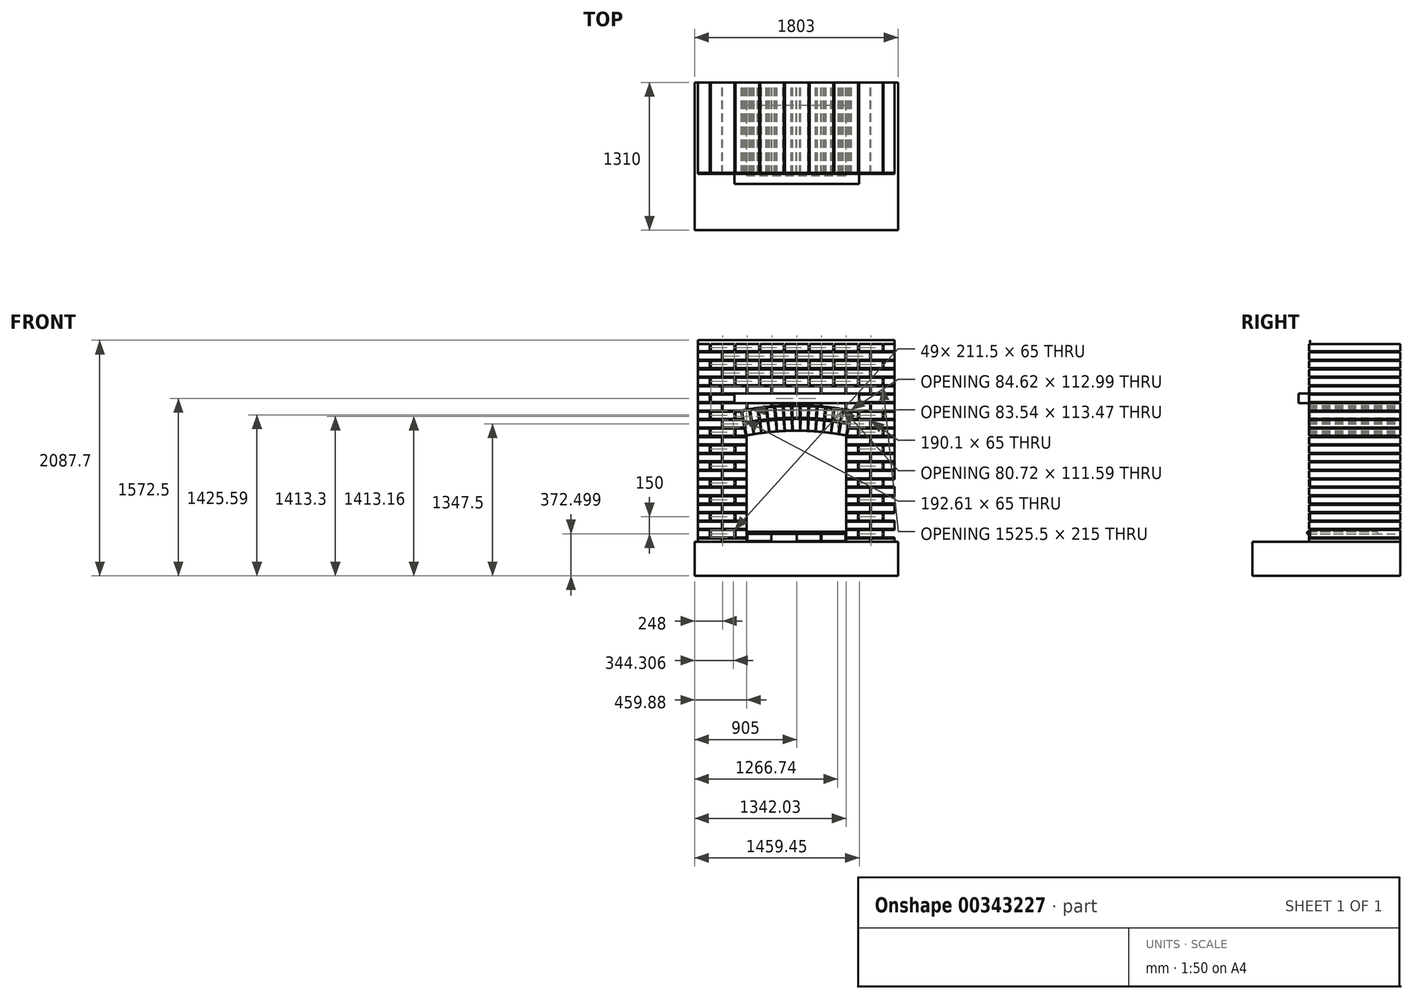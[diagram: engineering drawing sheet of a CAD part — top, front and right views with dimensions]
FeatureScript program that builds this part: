
annotation { "Feature Type Name" : "Feature", "Feature Type Description" : "" }
export const myFeature = defineFeature(function(context is Context, id is Id, definition is map)
    precondition{}
    {
        {
            var Q0;
            Q0=qCreatedBy(makeId("Front.planeOp"),FACE);
            var sketch = newSketch(context, id + "F0", { "sketchPlane" : qUnion([Q0])});
            skArc(sketch, "E0", {"start": v(-257.23, 343.57) * mm, "mid": v(-289.53, 339.93) * mm, "end": v(-321.78, 335.87) * mm});
            skArc(sketch, "E1", {"start": v(316.65, 324.44) * mm, "mid": v(284.4, 328.46) * mm, "end": v(252.09, 332.04) * mm});
            skArc(sketch, "E2", {"start": v(461.03, 301.03) * mm, "mid": v(428.59, 307.07) * mm, "end": v(396.06, 312.67) * mm});
            skArc(sketch, "E3", {"start": v(463.3, 312.82) * mm, "mid": v(430.8, 318.87) * mm, "end": v(398.22, 324.48) * mm});
            skLineSegment(sketch, "E4", {"start": v(547.25, 196.15) * mm, "end": v(448.41, 196.15) * mm});
            skLineSegment(sketch, "E5", {"start": v(547.25, 346.15) * mm, "end": v(477.38, 346.15) * mm});
            skLineSegment(sketch, "E6", {"start": v(901.5, -743.85) * mm, "end": v(-901.5, -743.85) * mm});
            skLineSegment(sketch, "E7", {"start": v(-872.5, -743.85) * mm, "end": v(-872.5, 1043.85) * mm});
            skLineSegment(sketch, "E8", {"start": v(901.5, -1043.85) * mm, "end": v(901.5, -743.85) * mm});
            skLineSegment(sketch, "E9", {"start": v(-901.5, -1043.85) * mm, "end": v(-901.5, -743.85) * mm});
            skLineSegment(sketch, "E10", {"start": v(901.5, -1043.85) * mm, "end": v(-901.5, -1043.85) * mm});
            skArc(sketch, "E11", {"start": v(441.5, 199.9) * mm, "mid": v(-0.25, 242.15) * mm, "end": v(-442, 199.8) * mm});
            skLineSegment(sketch, "E12", {"start": v(-75, 136.15) * mm, "end": v(-75, 240.94) * mm});
            skLineSegment(sketch, "E13", {"start": v(75, 136.15) * mm, "end": v(75, 240.94) * mm});
            skLineSegment(sketch, "E14", {"start": v(-661, 871.15) * mm, "end": v(-872.5, 871.15) * mm});
            skLineSegment(sketch, "E15", {"start": v(-442, 871.15) * mm, "end": v(-653.5, 871.15) * mm});
            skLineSegment(sketch, "E16", {"start": v(-661, 936.15) * mm, "end": v(-872.5, 936.15) * mm});
            skLineSegment(sketch, "E17", {"start": v(-442, 936.15) * mm, "end": v(-653.5, 936.15) * mm});
            skLineSegment(sketch, "E18", {"start": v(-223, 871.15) * mm, "end": v(-434.5, 871.15) * mm});
            skLineSegment(sketch, "E19", {"start": v(-4, 871.15) * mm, "end": v(-215.5, 871.15) * mm});
            skLineSegment(sketch, "E20", {"start": v(-223, 936.15) * mm, "end": v(-434.5, 936.15) * mm});
            skLineSegment(sketch, "E21", {"start": v(-4, 936.15) * mm, "end": v(-215.5, 936.15) * mm});
            skLineSegment(sketch, "E22", {"start": v(-661, 936.15) * mm, "end": v(-661, 871.15) * mm});
            skLineSegment(sketch, "E23", {"start": v(-653.5, 936.15) * mm, "end": v(-653.5, 871.15) * mm});
            skLineSegment(sketch, "E24", {"start": v(-442, 871.15) * mm, "end": v(-442, 936.15) * mm});
            skLineSegment(sketch, "E25", {"start": v(-434.5, 871.15) * mm, "end": v(-434.5, 936.15) * mm});
            skLineSegment(sketch, "E26", {"start": v(-223, 871.15) * mm, "end": v(-223, 936.15) * mm});
            skLineSegment(sketch, "E27", {"start": v(-215.5, 871.15) * mm, "end": v(-215.5, 936.15) * mm});
            skLineSegment(sketch, "E28", {"start": v(-4, 871.15) * mm, "end": v(-4, 936.15) * mm});
            skLineSegment(sketch, "E29", {"start": v(3.5, 871.15) * mm, "end": v(3.5, 936.15) * mm});
            skLineSegment(sketch, "E30", {"start": v(-766.75, 946.15) * mm, "end": v(-872.5, 946.15) * mm});
            skLineSegment(sketch, "E31", {"start": v(-547.75, 946.15) * mm, "end": v(-759.25, 946.15) * mm});
            skLineSegment(sketch, "E32", {"start": v(-766.75, 1011.15) * mm, "end": v(-872.5, 1011.15) * mm});
            skLineSegment(sketch, "E33", {"start": v(-547.75, 1011.15) * mm, "end": v(-759.25, 1011.15) * mm});
            skLineSegment(sketch, "E34", {"start": v(-328.75, 946.15) * mm, "end": v(-540.25, 946.15) * mm});
            skLineSegment(sketch, "E35", {"start": v(-109.75, 946.15) * mm, "end": v(-321.25, 946.15) * mm});
            skLineSegment(sketch, "E36", {"start": v(-328.75, 1011.15) * mm, "end": v(-540.25, 1011.15) * mm});
            skLineSegment(sketch, "E37", {"start": v(-109.75, 1011.15) * mm, "end": v(-321.25, 1011.15) * mm});
            skLineSegment(sketch, "E38", {"start": v(-766.75, 1011.15) * mm, "end": v(-766.75, 946.15) * mm});
            skLineSegment(sketch, "E39", {"start": v(-759.25, 1011.15) * mm, "end": v(-759.25, 946.15) * mm});
            skLineSegment(sketch, "E40", {"start": v(-547.75, 946.15) * mm, "end": v(-547.75, 1011.15) * mm});
            skLineSegment(sketch, "E41", {"start": v(-540.25, 946.15) * mm, "end": v(-540.25, 1011.15) * mm});
            skLineSegment(sketch, "E42", {"start": v(-328.75, 946.15) * mm, "end": v(-328.75, 1011.15) * mm});
            skLineSegment(sketch, "E43", {"start": v(-321.25, 946.15) * mm, "end": v(-321.25, 1011.15) * mm});
            skLineSegment(sketch, "E44", {"start": v(-109.75, 946.15) * mm, "end": v(-109.75, 1011.15) * mm});
            skLineSegment(sketch, "E45", {"start": v(-102.25, 946.15) * mm, "end": v(-102.25, 1011.15) * mm});
            skLineSegment(sketch, "E46", {"start": v(-661, 721.15) * mm, "end": v(-872.5, 721.15) * mm});
            skLineSegment(sketch, "E47", {"start": v(-442, 721.15) * mm, "end": v(-653.5, 721.15) * mm});
            skLineSegment(sketch, "E48", {"start": v(-661, 786.15) * mm, "end": v(-872.5, 786.15) * mm});
            skLineSegment(sketch, "E49", {"start": v(-442, 786.15) * mm, "end": v(-653.5, 786.15) * mm});
            skLineSegment(sketch, "E50", {"start": v(-223, 721.15) * mm, "end": v(-434.5, 721.15) * mm});
            skLineSegment(sketch, "E51", {"start": v(-4, 721.15) * mm, "end": v(-215.5, 721.15) * mm});
            skLineSegment(sketch, "E52", {"start": v(-223, 786.15) * mm, "end": v(-434.5, 786.15) * mm});
            skLineSegment(sketch, "E53", {"start": v(-4, 786.15) * mm, "end": v(-215.5, 786.15) * mm});
            skLineSegment(sketch, "E54", {"start": v(-661, 786.15) * mm, "end": v(-661, 721.15) * mm});
            skLineSegment(sketch, "E55", {"start": v(-653.5, 786.15) * mm, "end": v(-653.5, 721.15) * mm});
            skLineSegment(sketch, "E56", {"start": v(-442, 721.15) * mm, "end": v(-442, 786.15) * mm});
            skLineSegment(sketch, "E57", {"start": v(-434.5, 721.15) * mm, "end": v(-434.5, 786.15) * mm});
            skLineSegment(sketch, "E58", {"start": v(-223, 721.15) * mm, "end": v(-223, 786.15) * mm});
            skLineSegment(sketch, "E59", {"start": v(-215.5, 721.15) * mm, "end": v(-215.5, 786.15) * mm});
            skLineSegment(sketch, "E60", {"start": v(-4, 721.15) * mm, "end": v(-4, 786.15) * mm});
            skLineSegment(sketch, "E61", {"start": v(3.5, 721.15) * mm, "end": v(3.5, 786.15) * mm});
            skLineSegment(sketch, "E62", {"start": v(-766.75, 796.15) * mm, "end": v(-872.5, 796.15) * mm});
            skLineSegment(sketch, "E63", {"start": v(-547.75, 796.15) * mm, "end": v(-759.25, 796.15) * mm});
            skLineSegment(sketch, "E64", {"start": v(-547.75, 861.15) * mm, "end": v(-759.25, 861.15) * mm});
            skLineSegment(sketch, "E65", {"start": v(-328.75, 796.15) * mm, "end": v(-540.25, 796.15) * mm});
            skLineSegment(sketch, "E66", {"start": v(-109.75, 796.15) * mm, "end": v(-321.25, 796.15) * mm});
            skLineSegment(sketch, "E67", {"start": v(-328.75, 861.15) * mm, "end": v(-540.25, 861.15) * mm});
            skLineSegment(sketch, "E68", {"start": v(-109.75, 861.15) * mm, "end": v(-321.25, 861.15) * mm});
            skLineSegment(sketch, "E69", {"start": v(-766.75, 861.15) * mm, "end": v(-766.75, 796.15) * mm});
            skLineSegment(sketch, "E70", {"start": v(-759.25, 861.15) * mm, "end": v(-759.25, 796.15) * mm});
            skLineSegment(sketch, "E71", {"start": v(-547.75, 796.15) * mm, "end": v(-547.75, 861.15) * mm});
            skLineSegment(sketch, "E72", {"start": v(-540.25, 796.15) * mm, "end": v(-540.25, 861.15) * mm});
            skLineSegment(sketch, "E73", {"start": v(-328.75, 796.15) * mm, "end": v(-328.75, 861.15) * mm});
            skLineSegment(sketch, "E74", {"start": v(-321.25, 796.15) * mm, "end": v(-321.25, 861.15) * mm});
            skLineSegment(sketch, "E75", {"start": v(-109.75, 796.15) * mm, "end": v(-109.75, 861.15) * mm});
            skLineSegment(sketch, "E76", {"start": v(-102.25, 796.15) * mm, "end": v(-102.25, 861.15) * mm});
            skLineSegment(sketch, "E77", {"start": v(215, 871.15) * mm, "end": v(3.5, 871.15) * mm});
            skLineSegment(sketch, "E78", {"start": v(434, 871.15) * mm, "end": v(222.5, 871.15) * mm});
            skLineSegment(sketch, "E79", {"start": v(215, 936.15) * mm, "end": v(3.5, 936.15) * mm});
            skLineSegment(sketch, "E80", {"start": v(434, 936.15) * mm, "end": v(222.5, 936.15) * mm});
            skLineSegment(sketch, "E81", {"start": v(653, 871.15) * mm, "end": v(441.5, 871.15) * mm});
            skLineSegment(sketch, "E82", {"start": v(872, 871.15) * mm, "end": v(660.5, 871.15) * mm});
            skLineSegment(sketch, "E83", {"start": v(653, 936.15) * mm, "end": v(441.5, 936.15) * mm});
            skLineSegment(sketch, "E84", {"start": v(872, 936.15) * mm, "end": v(660.5, 936.15) * mm});
            skLineSegment(sketch, "E85", {"start": v(215, 936.15) * mm, "end": v(215, 871.15) * mm});
            skLineSegment(sketch, "E86", {"start": v(222.5, 936.15) * mm, "end": v(222.5, 871.15) * mm});
            skLineSegment(sketch, "E87", {"start": v(434, 871.15) * mm, "end": v(434, 936.15) * mm});
            skLineSegment(sketch, "E88", {"start": v(441.5, 871.15) * mm, "end": v(441.5, 936.15) * mm});
            skLineSegment(sketch, "E89", {"start": v(653, 871.15) * mm, "end": v(653, 936.15) * mm});
            skLineSegment(sketch, "E90", {"start": v(660.5, 871.15) * mm, "end": v(660.5, 936.15) * mm});
            skLineSegment(sketch, "E91", {"start": v(872, 871.15) * mm, "end": v(872, 936.15) * mm});
            skLineSegment(sketch, "E92", {"start": v(109.25, 946.15) * mm, "end": v(-102.25, 946.15) * mm});
            skLineSegment(sketch, "E93", {"start": v(328.25, 946.15) * mm, "end": v(116.75, 946.15) * mm});
            skLineSegment(sketch, "E94", {"start": v(109.25, 1011.15) * mm, "end": v(-102.25, 1011.15) * mm});
            skLineSegment(sketch, "E95", {"start": v(328.25, 1011.15) * mm, "end": v(116.75, 1011.15) * mm});
            skLineSegment(sketch, "E96", {"start": v(547.25, 946.15) * mm, "end": v(335.75, 946.15) * mm});
            skLineSegment(sketch, "E97", {"start": v(766.25, 946.15) * mm, "end": v(554.75, 946.15) * mm});
            skLineSegment(sketch, "E98", {"start": v(547.25, 1011.15) * mm, "end": v(335.75, 1011.15) * mm});
            skLineSegment(sketch, "E99", {"start": v(766.25, 1011.15) * mm, "end": v(554.75, 1011.15) * mm});
            skLineSegment(sketch, "E100", {"start": v(109.25, 1011.15) * mm, "end": v(109.25, 946.15) * mm});
            skLineSegment(sketch, "E101", {"start": v(116.75, 1011.15) * mm, "end": v(116.75, 946.15) * mm});
            skLineSegment(sketch, "E102", {"start": v(328.25, 946.15) * mm, "end": v(328.25, 1011.15) * mm});
            skLineSegment(sketch, "E103", {"start": v(335.75, 946.15) * mm, "end": v(335.75, 1011.15) * mm});
            skLineSegment(sketch, "E104", {"start": v(547.25, 946.15) * mm, "end": v(547.25, 1011.15) * mm});
            skLineSegment(sketch, "E105", {"start": v(554.75, 946.15) * mm, "end": v(554.75, 1011.15) * mm});
            skLineSegment(sketch, "E106", {"start": v(766.25, 946.15) * mm, "end": v(766.25, 1011.15) * mm});
            skLineSegment(sketch, "E107", {"start": v(773.75, 946.15) * mm, "end": v(773.75, 1011.15) * mm});
            skLineSegment(sketch, "E108", {"start": v(215, 861.15) * mm, "end": v(3.5, 861.15) * mm});
            skLineSegment(sketch, "E109", {"start": v(215, 721.15) * mm, "end": v(3.5, 721.15) * mm});
            skLineSegment(sketch, "E110", {"start": v(434, 721.15) * mm, "end": v(222.5, 721.15) * mm});
            skLineSegment(sketch, "E111", {"start": v(215, 786.15) * mm, "end": v(3.5, 786.15) * mm});
            skLineSegment(sketch, "E112", {"start": v(434, 786.15) * mm, "end": v(222.5, 786.15) * mm});
            skLineSegment(sketch, "E113", {"start": v(653, 721.15) * mm, "end": v(441.5, 721.15) * mm});
            skLineSegment(sketch, "E114", {"start": v(872, 721.15) * mm, "end": v(660.5, 721.15) * mm});
            skLineSegment(sketch, "E115", {"start": v(653, 786.15) * mm, "end": v(441.5, 786.15) * mm});
            skLineSegment(sketch, "E116", {"start": v(872, 786.15) * mm, "end": v(660.5, 786.15) * mm});
            skLineSegment(sketch, "E117", {"start": v(215, 786.15) * mm, "end": v(215, 721.15) * mm});
            skLineSegment(sketch, "E118", {"start": v(222.5, 786.15) * mm, "end": v(222.5, 721.15) * mm});
            skLineSegment(sketch, "E119", {"start": v(434, 721.15) * mm, "end": v(434, 786.15) * mm});
            skLineSegment(sketch, "E120", {"start": v(441.5, 721.15) * mm, "end": v(441.5, 786.15) * mm});
            skLineSegment(sketch, "E121", {"start": v(653, 721.15) * mm, "end": v(653, 786.15) * mm});
            skLineSegment(sketch, "E122", {"start": v(660.5, 721.15) * mm, "end": v(660.5, 786.15) * mm});
            skLineSegment(sketch, "E123", {"start": v(872, 721.15) * mm, "end": v(872, 786.15) * mm});
            skLineSegment(sketch, "E124", {"start": v(109.25, 796.15) * mm, "end": v(-102.25, 796.15) * mm});
            skLineSegment(sketch, "E125", {"start": v(328.25, 796.15) * mm, "end": v(116.75, 796.15) * mm});
            skLineSegment(sketch, "E126", {"start": v(109.25, 861.15) * mm, "end": v(-102.25, 861.15) * mm});
            skLineSegment(sketch, "E127", {"start": v(328.25, 861.15) * mm, "end": v(116.75, 861.15) * mm});
            skLineSegment(sketch, "E128", {"start": v(547.25, 796.15) * mm, "end": v(335.75, 796.15) * mm});
            skLineSegment(sketch, "E129", {"start": v(766.25, 796.15) * mm, "end": v(554.75, 796.15) * mm});
            skLineSegment(sketch, "E130", {"start": v(547.25, 861.15) * mm, "end": v(335.75, 861.15) * mm});
            skLineSegment(sketch, "E131", {"start": v(766.25, 861.15) * mm, "end": v(554.75, 861.15) * mm});
            skLineSegment(sketch, "E132", {"start": v(109.25, 861.15) * mm, "end": v(109.25, 796.15) * mm});
            skLineSegment(sketch, "E133", {"start": v(116.75, 861.15) * mm, "end": v(116.75, 796.15) * mm});
            skLineSegment(sketch, "E134", {"start": v(328.25, 796.15) * mm, "end": v(328.25, 861.15) * mm});
            skLineSegment(sketch, "E135", {"start": v(335.75, 796.15) * mm, "end": v(335.75, 861.15) * mm});
            skLineSegment(sketch, "E136", {"start": v(547.25, 796.15) * mm, "end": v(547.25, 861.15) * mm});
            skLineSegment(sketch, "E137", {"start": v(554.75, 796.15) * mm, "end": v(554.75, 861.15) * mm});
            skLineSegment(sketch, "E138", {"start": v(766.25, 796.15) * mm, "end": v(766.25, 861.15) * mm});
            skLineSegment(sketch, "E139", {"start": v(773.75, 796.15) * mm, "end": v(773.75, 861.15) * mm});
            skLineSegment(sketch, "E140", {"start": v(-766.75, 861.15) * mm, "end": v(-872.5, 861.15) * mm});
            skLineSegment(sketch, "E141", {"start": v(773.75, 1011.15) * mm, "end": v(872, 1011.15) * mm});
            skLineSegment(sketch, "E142", {"start": v(773.75, 946.15) * mm, "end": v(872, 946.15) * mm});
            skLineSegment(sketch, "E143", {"start": v(773.75, 861.15) * mm, "end": v(872.5, 861.15) * mm});
            skLineSegment(sketch, "E144", {"start": v(773.75, 796.15) * mm, "end": v(872, 796.15) * mm});
            skLineSegment(sketch, "E145", {"start": v(-661, 571.15) * mm, "end": v(-872.5, 571.15) * mm});
            skLineSegment(sketch, "E146", {"start": v(-442, 571.15) * mm, "end": v(-653.5, 571.15) * mm});
            skLineSegment(sketch, "E147", {"start": v(-661, 636.15) * mm, "end": v(-872.5, 636.15) * mm});
            skLineSegment(sketch, "E148", {"start": v(-442, 636.15) * mm, "end": v(-653.5, 636.15) * mm});
            skLineSegment(sketch, "E149", {"start": v(-223, 571.15) * mm, "end": v(-434.5, 571.15) * mm});
            skLineSegment(sketch, "E150", {"start": v(-4, 571.15) * mm, "end": v(-215.5, 571.15) * mm});
            skLineSegment(sketch, "E151", {"start": v(-223, 636.15) * mm, "end": v(-434.5, 636.15) * mm});
            skLineSegment(sketch, "E152", {"start": v(-4, 636.15) * mm, "end": v(-215.5, 636.15) * mm});
            skLineSegment(sketch, "E153", {"start": v(-661, 636.15) * mm, "end": v(-661, 571.15) * mm});
            skLineSegment(sketch, "E154", {"start": v(-653.5, 636.15) * mm, "end": v(-653.5, 571.15) * mm});
            skLineSegment(sketch, "E155", {"start": v(-442, 571.15) * mm, "end": v(-442, 636.15) * mm});
            skLineSegment(sketch, "E156", {"start": v(-434.5, 571.15) * mm, "end": v(-434.5, 636.15) * mm});
            skLineSegment(sketch, "E157", {"start": v(-223, 571.15) * mm, "end": v(-223, 636.15) * mm});
            skLineSegment(sketch, "E158", {"start": v(-215.5, 571.15) * mm, "end": v(-215.5, 636.15) * mm});
            skLineSegment(sketch, "E159", {"start": v(-4, 571.15) * mm, "end": v(-4, 636.15) * mm});
            skLineSegment(sketch, "E160", {"start": v(3.5, 571.15) * mm, "end": v(3.5, 636.15) * mm});
            skLineSegment(sketch, "E161", {"start": v(-766.75, 646.15) * mm, "end": v(-872.5, 646.15) * mm});
            skLineSegment(sketch, "E162", {"start": v(-547.75, 646.15) * mm, "end": v(-759.25, 646.15) * mm});
            skLineSegment(sketch, "E163", {"start": v(-766.75, 711.15) * mm, "end": v(-872.5, 711.15) * mm});
            skLineSegment(sketch, "E164", {"start": v(-547.75, 711.15) * mm, "end": v(-759.25, 711.15) * mm});
            skLineSegment(sketch, "E165", {"start": v(-328.75, 646.15) * mm, "end": v(-540.25, 646.15) * mm});
            skLineSegment(sketch, "E166", {"start": v(-109.75, 646.15) * mm, "end": v(-321.25, 646.15) * mm});
            skLineSegment(sketch, "E167", {"start": v(-328.75, 711.15) * mm, "end": v(-540.25, 711.15) * mm});
            skLineSegment(sketch, "E168", {"start": v(-109.75, 711.15) * mm, "end": v(-321.25, 711.15) * mm});
            skLineSegment(sketch, "E169", {"start": v(-766.75, 711.15) * mm, "end": v(-766.75, 646.15) * mm});
            skLineSegment(sketch, "E170", {"start": v(-759.25, 711.15) * mm, "end": v(-759.25, 646.15) * mm});
            skLineSegment(sketch, "E171", {"start": v(-547.75, 646.15) * mm, "end": v(-547.75, 711.15) * mm});
            skLineSegment(sketch, "E172", {"start": v(-540.25, 646.15) * mm, "end": v(-540.25, 711.15) * mm});
            skLineSegment(sketch, "E173", {"start": v(-328.75, 646.15) * mm, "end": v(-328.75, 711.15) * mm});
            skLineSegment(sketch, "E174", {"start": v(-321.25, 646.15) * mm, "end": v(-321.25, 711.15) * mm});
            skLineSegment(sketch, "E175", {"start": v(-109.75, 646.15) * mm, "end": v(-109.75, 711.15) * mm});
            skLineSegment(sketch, "E176", {"start": v(-102.25, 646.15) * mm, "end": v(-102.25, 711.15) * mm});
            skLineSegment(sketch, "E177", {"start": v(-661, 421.15) * mm, "end": v(-872.5, 421.15) * mm});
            skLineSegment(sketch, "E178", {"start": v(-485.1, 421.15) * mm, "end": v(-653.5, 421.15) * mm});
            skLineSegment(sketch, "E179", {"start": v(-661, 486.15) * mm, "end": v(-872.5, 486.15) * mm});
            skLineSegment(sketch, "E180", {"start": v(-442, 486.15) * mm, "end": v(-653.5, 486.15) * mm});
            skLineSegment(sketch, "E181", {"start": v(-223, 486.15) * mm, "end": v(-434.5, 486.15) * mm});
            skLineSegment(sketch, "E182", {"start": v(-4, 486.15) * mm, "end": v(-215.5, 486.15) * mm});
            skLineSegment(sketch, "E183", {"start": v(-661, 486.15) * mm, "end": v(-661, 421.15) * mm});
            skLineSegment(sketch, "E184", {"start": v(-653.5, 486.15) * mm, "end": v(-653.5, 421.15) * mm});
            skLineSegment(sketch, "E185", {"start": v(-442, 429.1) * mm, "end": v(-442, 486.15) * mm});
            skLineSegment(sketch, "E186", {"start": v(-434.5, 430.41) * mm, "end": v(-434.5, 486.15) * mm});
            skLineSegment(sketch, "E187", {"start": v(-223, 457.9) * mm, "end": v(-223, 486.15) * mm});
            skLineSegment(sketch, "E188", {"start": v(-215.5, 458.54) * mm, "end": v(-215.5, 486.15) * mm});
            skLineSegment(sketch, "E189", {"start": v(-4, 467.65) * mm, "end": v(-4, 486.15) * mm});
            skLineSegment(sketch, "E190", {"start": v(3.5, 467.65) * mm, "end": v(3.5, 486.15) * mm});
            skLineSegment(sketch, "E191", {"start": v(-766.75, 496.15) * mm, "end": v(-872.5, 496.15) * mm});
            skLineSegment(sketch, "E192", {"start": v(-547.75, 496.15) * mm, "end": v(-759.25, 496.15) * mm});
            skLineSegment(sketch, "E193", {"start": v(-547.75, 561.15) * mm, "end": v(-759.25, 561.15) * mm});
            skLineSegment(sketch, "E194", {"start": v(-766.75, 561.15) * mm, "end": v(-766.75, 496.15) * mm});
            skLineSegment(sketch, "E195", {"start": v(-759.25, 561.15) * mm, "end": v(-759.25, 496.15) * mm});
            skLineSegment(sketch, "E196", {"start": v(-547.75, 496.15) * mm, "end": v(-547.75, 561.15) * mm});
            skLineSegment(sketch, "E197", {"start": v(215, 571.15) * mm, "end": v(3.5, 571.15) * mm});
            skLineSegment(sketch, "E198", {"start": v(434, 571.15) * mm, "end": v(222.5, 571.15) * mm});
            skLineSegment(sketch, "E199", {"start": v(215, 636.15) * mm, "end": v(3.5, 636.15) * mm});
            skLineSegment(sketch, "E200", {"start": v(434, 636.15) * mm, "end": v(222.5, 636.15) * mm});
            skLineSegment(sketch, "E201", {"start": v(653, 571.15) * mm, "end": v(441.5, 571.15) * mm});
            skLineSegment(sketch, "E202", {"start": v(872, 571.15) * mm, "end": v(660.5, 571.15) * mm});
            skLineSegment(sketch, "E203", {"start": v(653, 636.15) * mm, "end": v(441.5, 636.15) * mm});
            skLineSegment(sketch, "E204", {"start": v(872, 636.15) * mm, "end": v(660.5, 636.15) * mm});
            skLineSegment(sketch, "E205", {"start": v(215, 636.15) * mm, "end": v(215, 571.15) * mm});
            skLineSegment(sketch, "E206", {"start": v(222.5, 636.15) * mm, "end": v(222.5, 571.15) * mm});
            skLineSegment(sketch, "E207", {"start": v(434, 571.15) * mm, "end": v(434, 636.15) * mm});
            skLineSegment(sketch, "E208", {"start": v(441.5, 571.15) * mm, "end": v(441.5, 636.15) * mm});
            skLineSegment(sketch, "E209", {"start": v(653, 571.15) * mm, "end": v(653, 636.15) * mm});
            skLineSegment(sketch, "E210", {"start": v(660.5, 571.15) * mm, "end": v(660.5, 636.15) * mm});
            skLineSegment(sketch, "E211", {"start": v(872, 571.15) * mm, "end": v(872, 636.15) * mm});
            skLineSegment(sketch, "E212", {"start": v(109.25, 646.15) * mm, "end": v(-102.25, 646.15) * mm});
            skLineSegment(sketch, "E213", {"start": v(328.25, 646.15) * mm, "end": v(116.75, 646.15) * mm});
            skLineSegment(sketch, "E214", {"start": v(109.25, 711.15) * mm, "end": v(-102.25, 711.15) * mm});
            skLineSegment(sketch, "E215", {"start": v(328.25, 711.15) * mm, "end": v(116.75, 711.15) * mm});
            skLineSegment(sketch, "E216", {"start": v(547.25, 646.15) * mm, "end": v(335.75, 646.15) * mm});
            skLineSegment(sketch, "E217", {"start": v(766.25, 646.15) * mm, "end": v(554.75, 646.15) * mm});
            skLineSegment(sketch, "E218", {"start": v(547.25, 711.15) * mm, "end": v(335.75, 711.15) * mm});
            skLineSegment(sketch, "E219", {"start": v(766.25, 711.15) * mm, "end": v(554.75, 711.15) * mm});
            skLineSegment(sketch, "E220", {"start": v(109.25, 711.15) * mm, "end": v(109.25, 646.15) * mm});
            skLineSegment(sketch, "E221", {"start": v(116.75, 711.15) * mm, "end": v(116.75, 646.15) * mm});
            skLineSegment(sketch, "E222", {"start": v(328.25, 646.15) * mm, "end": v(328.25, 711.15) * mm});
            skLineSegment(sketch, "E223", {"start": v(335.75, 646.15) * mm, "end": v(335.75, 711.15) * mm});
            skLineSegment(sketch, "E224", {"start": v(547.25, 646.15) * mm, "end": v(547.25, 711.15) * mm});
            skLineSegment(sketch, "E225", {"start": v(554.75, 646.15) * mm, "end": v(554.75, 711.15) * mm});
            skLineSegment(sketch, "E226", {"start": v(766.25, 646.15) * mm, "end": v(766.25, 711.15) * mm});
            skLineSegment(sketch, "E227", {"start": v(773.75, 646.15) * mm, "end": v(773.75, 711.15) * mm});
            skLineSegment(sketch, "E228", {"start": v(215, 486.15) * mm, "end": v(3.5, 486.15) * mm});
            skLineSegment(sketch, "E229", {"start": v(434, 486.15) * mm, "end": v(222.5, 486.15) * mm});
            skLineSegment(sketch, "E230", {"start": v(653, 421.15) * mm, "end": v(485.1, 421.15) * mm});
            skLineSegment(sketch, "E231", {"start": v(872, 421.15) * mm, "end": v(660.5, 421.15) * mm});
            skLineSegment(sketch, "E232", {"start": v(653, 486.15) * mm, "end": v(441.5, 486.15) * mm});
            skLineSegment(sketch, "E233", {"start": v(872, 486.15) * mm, "end": v(660.5, 486.15) * mm});
            skLineSegment(sketch, "E234", {"start": v(215, 486.15) * mm, "end": v(215, 458.58) * mm});
            skLineSegment(sketch, "E235", {"start": v(222.5, 486.15) * mm, "end": v(222.5, 457.94) * mm});
            skLineSegment(sketch, "E236", {"start": v(434, 430.5) * mm, "end": v(434, 486.15) * mm});
            skLineSegment(sketch, "E237", {"start": v(441.5, 429.2) * mm, "end": v(441.5, 486.15) * mm});
            skLineSegment(sketch, "E238", {"start": v(653, 421.15) * mm, "end": v(653, 486.15) * mm});
            skLineSegment(sketch, "E239", {"start": v(660.5, 421.15) * mm, "end": v(660.5, 486.15) * mm});
            skLineSegment(sketch, "E240", {"start": v(872, 421.15) * mm, "end": v(872, 486.15) * mm});
            skLineSegment(sketch, "E241", {"start": v(766.25, 496.15) * mm, "end": v(554.75, 496.15) * mm});
            skLineSegment(sketch, "E242", {"start": v(766.25, 561.15) * mm, "end": v(554.75, 561.15) * mm});
            skLineSegment(sketch, "E243", {"start": v(554.75, 496.15) * mm, "end": v(554.75, 561.15) * mm});
            skLineSegment(sketch, "E244", {"start": v(766.25, 496.15) * mm, "end": v(766.25, 561.15) * mm});
            skLineSegment(sketch, "E245", {"start": v(773.75, 496.15) * mm, "end": v(773.75, 561.15) * mm});
            skLineSegment(sketch, "E246", {"start": v(-766.75, 561.15) * mm, "end": v(-872.5, 561.15) * mm});
            skLineSegment(sketch, "E247", {"start": v(773.75, 711.15) * mm, "end": v(872, 711.15) * mm});
            skLineSegment(sketch, "E248", {"start": v(773.75, 646.15) * mm, "end": v(872, 646.15) * mm});
            skLineSegment(sketch, "E249", {"start": v(773.75, 561.15) * mm, "end": v(872.5, 561.15) * mm});
            skLineSegment(sketch, "E250", {"start": v(773.75, 496.15) * mm, "end": v(872, 496.15) * mm});
            skLineSegment(sketch, "E251", {"start": v(-661, 271.15) * mm, "end": v(-872.5, 271.15) * mm});
            skLineSegment(sketch, "E252", {"start": v(-460.89, 271.15) * mm, "end": v(-653.5, 271.15) * mm});
            skLineSegment(sketch, "E253", {"start": v(-661, 336.15) * mm, "end": v(-872.5, 336.15) * mm});
            skLineSegment(sketch, "E254", {"start": v(-473.46, 336.15) * mm, "end": v(-653.5, 336.15) * mm});
            skLineSegment(sketch, "E255", {"start": v(-661, 336.15) * mm, "end": v(-661, 271.15) * mm});
            skLineSegment(sketch, "E256", {"start": v(-653.5, 336.15) * mm, "end": v(-653.5, 271.15) * mm});
            skLineSegment(sketch, "E257", {"start": v(-766.75, 346.15) * mm, "end": v(-872.5, 346.15) * mm});
            skLineSegment(sketch, "E258", {"start": v(-547.75, 346.15) * mm, "end": v(-759.25, 346.15) * mm});
            skLineSegment(sketch, "E259", {"start": v(-766.75, 411.15) * mm, "end": v(-872.5, 411.15) * mm});
            skLineSegment(sketch, "E260", {"start": v(-547.75, 411.15) * mm, "end": v(-759.25, 411.15) * mm});
            skLineSegment(sketch, "E261", {"start": v(-475.4, 346.15) * mm, "end": v(-540.25, 346.15) * mm});
            skLineSegment(sketch, "E262", {"start": v(-487.96, 411.15) * mm, "end": v(-540.25, 411.15) * mm});
            skLineSegment(sketch, "E263", {"start": v(-766.75, 411.15) * mm, "end": v(-766.75, 346.15) * mm});
            skLineSegment(sketch, "E264", {"start": v(-759.25, 411.15) * mm, "end": v(-759.25, 346.15) * mm});
            skLineSegment(sketch, "E265", {"start": v(-547.75, 346.15) * mm, "end": v(-547.75, 411.15) * mm});
            skLineSegment(sketch, "E266", {"start": v(-540.25, 346.15) * mm, "end": v(-540.25, 411.15) * mm});
            skLineSegment(sketch, "E267", {"start": v(-661, 121.15) * mm, "end": v(-872.5, 121.15) * mm});
            skLineSegment(sketch, "E268", {"start": v(-442, 121.15) * mm, "end": v(-653.5, 121.15) * mm});
            skLineSegment(sketch, "E269", {"start": v(-661, 186.15) * mm, "end": v(-872.5, 186.15) * mm});
            skLineSegment(sketch, "E270", {"start": v(-442, 186.15) * mm, "end": v(-653.5, 186.15) * mm});
            skLineSegment(sketch, "E271", {"start": v(-661, 186.15) * mm, "end": v(-661, 121.15) * mm});
            skLineSegment(sketch, "E272", {"start": v(-653.5, 186.15) * mm, "end": v(-653.5, 121.15) * mm});
            skLineSegment(sketch, "E273", {"start": v(-766.75, 196.15) * mm, "end": v(-872.5, 196.15) * mm});
            skLineSegment(sketch, "E274", {"start": v(-547.75, 196.15) * mm, "end": v(-759.25, 196.15) * mm});
            skLineSegment(sketch, "E275", {"start": v(-547.75, 261.15) * mm, "end": v(-759.25, 261.15) * mm});
            skLineSegment(sketch, "E276", {"start": v(-446.39, 196.15) * mm, "end": v(-540.25, 196.15) * mm});
            skLineSegment(sketch, "E277", {"start": v(-458.95, 261.15) * mm, "end": v(-540.25, 261.15) * mm});
            skLineSegment(sketch, "E278", {"start": v(-766.75, 261.15) * mm, "end": v(-766.75, 196.15) * mm});
            skLineSegment(sketch, "E279", {"start": v(-759.25, 261.15) * mm, "end": v(-759.25, 196.15) * mm});
            skLineSegment(sketch, "E280", {"start": v(-547.75, 196.15) * mm, "end": v(-547.75, 261.15) * mm});
            skLineSegment(sketch, "E281", {"start": v(-540.25, 196.15) * mm, "end": v(-540.25, 261.15) * mm});
            skLineSegment(sketch, "E282", {"start": v(653, 271.15) * mm, "end": v(462.9, 271.15) * mm});
            skLineSegment(sketch, "E283", {"start": v(872, 271.15) * mm, "end": v(660.5, 271.15) * mm});
            skLineSegment(sketch, "E284", {"start": v(653, 336.15) * mm, "end": v(475.45, 336.15) * mm});
            skLineSegment(sketch, "E285", {"start": v(872, 336.15) * mm, "end": v(660.5, 336.15) * mm});
            skLineSegment(sketch, "E286", {"start": v(653, 271.15) * mm, "end": v(653, 336.15) * mm});
            skLineSegment(sketch, "E287", {"start": v(660.5, 271.15) * mm, "end": v(660.5, 336.15) * mm});
            skLineSegment(sketch, "E288", {"start": v(872, 271.15) * mm, "end": v(872, 336.15) * mm});
            skLineSegment(sketch, "E289", {"start": v(766.25, 346.15) * mm, "end": v(554.75, 346.15) * mm});
            skLineSegment(sketch, "E290", {"start": v(547.25, 411.15) * mm, "end": v(489.94, 411.15) * mm});
            skLineSegment(sketch, "E291", {"start": v(766.25, 411.15) * mm, "end": v(554.75, 411.15) * mm});
            skLineSegment(sketch, "E292", {"start": v(547.25, 346.15) * mm, "end": v(547.25, 411.15) * mm});
            skLineSegment(sketch, "E293", {"start": v(554.75, 346.15) * mm, "end": v(554.75, 411.15) * mm});
            skLineSegment(sketch, "E294", {"start": v(766.25, 346.15) * mm, "end": v(766.25, 411.15) * mm});
            skLineSegment(sketch, "E295", {"start": v(773.75, 346.15) * mm, "end": v(773.75, 411.15) * mm});
            skLineSegment(sketch, "E296", {"start": v(653, 121.15) * mm, "end": v(441.5, 121.15) * mm});
            skLineSegment(sketch, "E297", {"start": v(872, 121.15) * mm, "end": v(660.5, 121.15) * mm});
            skLineSegment(sketch, "E298", {"start": v(653, 186.15) * mm, "end": v(441.5, 186.15) * mm});
            skLineSegment(sketch, "E299", {"start": v(872, 186.15) * mm, "end": v(660.5, 186.15) * mm});
            skLineSegment(sketch, "E300", {"start": v(441.5, 121.15) * mm, "end": v(441.5, 186.15) * mm});
            skLineSegment(sketch, "E301", {"start": v(653, 121.15) * mm, "end": v(653, 186.15) * mm});
            skLineSegment(sketch, "E302", {"start": v(660.5, 121.15) * mm, "end": v(660.5, 186.15) * mm});
            skLineSegment(sketch, "E303", {"start": v(872, 121.15) * mm, "end": v(872, 186.15) * mm});
            skLineSegment(sketch, "E304", {"start": v(766.25, 196.15) * mm, "end": v(554.75, 196.15) * mm});
            skLineSegment(sketch, "E305", {"start": v(547.25, 261.15) * mm, "end": v(460.97, 261.15) * mm});
            skLineSegment(sketch, "E306", {"start": v(766.25, 261.15) * mm, "end": v(554.75, 261.15) * mm});
            skLineSegment(sketch, "E307", {"start": v(547.25, 196.15) * mm, "end": v(547.25, 261.15) * mm});
            skLineSegment(sketch, "E308", {"start": v(554.75, 196.15) * mm, "end": v(554.75, 261.15) * mm});
            skLineSegment(sketch, "E309", {"start": v(766.25, 196.15) * mm, "end": v(766.25, 261.15) * mm});
            skLineSegment(sketch, "E310", {"start": v(773.75, 196.15) * mm, "end": v(773.75, 261.15) * mm});
            skLineSegment(sketch, "E311", {"start": v(-766.75, 261.15) * mm, "end": v(-872.5, 261.15) * mm});
            skLineSegment(sketch, "E312", {"start": v(773.75, 411.15) * mm, "end": v(872, 411.15) * mm});
            skLineSegment(sketch, "E313", {"start": v(773.75, 346.15) * mm, "end": v(872, 346.15) * mm});
            skLineSegment(sketch, "E314", {"start": v(773.75, 261.15) * mm, "end": v(872.5, 261.15) * mm});
            skLineSegment(sketch, "E315", {"start": v(773.75, 196.15) * mm, "end": v(872, 196.15) * mm});
            skLineSegment(sketch, "E316", {"start": v(-661, -28.85) * mm, "end": v(-872.5, -28.85) * mm});
            skLineSegment(sketch, "E317", {"start": v(-442, -28.85) * mm, "end": v(-653.5, -28.85) * mm});
            skLineSegment(sketch, "E318", {"start": v(-661, 36.15) * mm, "end": v(-872.5, 36.15) * mm});
            skLineSegment(sketch, "E319", {"start": v(-442, 36.15) * mm, "end": v(-653.5, 36.15) * mm});
            skLineSegment(sketch, "E320", {"start": v(-661, 36.15) * mm, "end": v(-661, -28.85) * mm});
            skLineSegment(sketch, "E321", {"start": v(-653.5, 36.15) * mm, "end": v(-653.5, -28.85) * mm});
            skLineSegment(sketch, "E322", {"start": v(-442, -28.85) * mm, "end": v(-442, 36.15) * mm});
            skLineSegment(sketch, "E323", {"start": v(-766.75, 46.15) * mm, "end": v(-872.5, 46.15) * mm});
            skLineSegment(sketch, "E324", {"start": v(-547.75, 46.15) * mm, "end": v(-759.25, 46.15) * mm});
            skLineSegment(sketch, "E325", {"start": v(-766.75, 111.15) * mm, "end": v(-872.5, 111.15) * mm});
            skLineSegment(sketch, "E326", {"start": v(-547.75, 111.15) * mm, "end": v(-759.25, 111.15) * mm});
            skLineSegment(sketch, "E327", {"start": v(-766.75, 111.15) * mm, "end": v(-766.75, 46.15) * mm});
            skLineSegment(sketch, "E328", {"start": v(-759.25, 111.15) * mm, "end": v(-759.25, 46.15) * mm});
            skLineSegment(sketch, "E329", {"start": v(-547.75, 46.15) * mm, "end": v(-547.75, 111.15) * mm});
            skLineSegment(sketch, "E330", {"start": v(-540.25, 46.15) * mm, "end": v(-540.25, 111.15) * mm});
            skLineSegment(sketch, "E331", {"start": v(-661, -178.85) * mm, "end": v(-872.5, -178.85) * mm});
            skLineSegment(sketch, "E332", {"start": v(-442, -178.85) * mm, "end": v(-653.5, -178.85) * mm});
            skLineSegment(sketch, "E333", {"start": v(-661, -113.85) * mm, "end": v(-872.5, -113.85) * mm});
            skLineSegment(sketch, "E334", {"start": v(-442, -113.85) * mm, "end": v(-653.5, -113.85) * mm});
            skLineSegment(sketch, "E335", {"start": v(-661, -113.85) * mm, "end": v(-661, -178.85) * mm});
            skLineSegment(sketch, "E336", {"start": v(-653.5, -113.85) * mm, "end": v(-653.5, -178.85) * mm});
            skLineSegment(sketch, "E337", {"start": v(-442, -178.85) * mm, "end": v(-442, -113.85) * mm});
            skLineSegment(sketch, "E338", {"start": v(-766.75, -103.85) * mm, "end": v(-872.5, -103.85) * mm});
            skLineSegment(sketch, "E339", {"start": v(-547.75, -103.85) * mm, "end": v(-759.25, -103.85) * mm});
            skLineSegment(sketch, "E340", {"start": v(-547.75, -38.85) * mm, "end": v(-759.25, -38.85) * mm});
            skLineSegment(sketch, "E341", {"start": v(-766.75, -38.85) * mm, "end": v(-766.75, -103.85) * mm});
            skLineSegment(sketch, "E342", {"start": v(-759.25, -38.85) * mm, "end": v(-759.25, -103.85) * mm});
            skLineSegment(sketch, "E343", {"start": v(-547.75, -103.85) * mm, "end": v(-547.75, -38.85) * mm});
            skLineSegment(sketch, "E344", {"start": v(-540.25, -103.85) * mm, "end": v(-540.25, -38.85) * mm});
            skLineSegment(sketch, "E345", {"start": v(872, 111.15) * mm, "end": v(773.25, 111.15) * mm});
            skLineSegment(sketch, "E346", {"start": v(872, 46.15) * mm, "end": v(872, 111.15) * mm});
            skLineSegment(sketch, "E347", {"start": v(765.75, 46.15) * mm, "end": v(554.25, 46.15) * mm});
            skLineSegment(sketch, "E348", {"start": v(765.75, 111.15) * mm, "end": v(554.25, 111.15) * mm});
            skLineSegment(sketch, "E349", {"start": v(546.75, 46.15) * mm, "end": v(546.75, 111.15) * mm});
            skLineSegment(sketch, "E350", {"start": v(554.25, 46.15) * mm, "end": v(554.25, 111.15) * mm});
            skLineSegment(sketch, "E351", {"start": v(765.75, 46.15) * mm, "end": v(765.75, 111.15) * mm});
            skLineSegment(sketch, "E352", {"start": v(773.25, 46.15) * mm, "end": v(773.25, 111.15) * mm});
            skLineSegment(sketch, "E353", {"start": v(-766.75, -38.85) * mm, "end": v(-872.5, -38.85) * mm});
            skLineSegment(sketch, "E354", {"start": v(773.25, 111.15) * mm, "end": v(872, 111.15) * mm});
            skLineSegment(sketch, "E355", {"start": v(773.25, 46.15) * mm, "end": v(871.5, 46.15) * mm});
            skLineSegment(sketch, "E356", {"start": v(-661, -328.85) * mm, "end": v(-872.5, -328.85) * mm});
            skLineSegment(sketch, "E357", {"start": v(-442, -328.85) * mm, "end": v(-653.5, -328.85) * mm});
            skLineSegment(sketch, "E358", {"start": v(-661, -263.85) * mm, "end": v(-872.5, -263.85) * mm});
            skLineSegment(sketch, "E359", {"start": v(-442, -263.85) * mm, "end": v(-653.5, -263.85) * mm});
            skLineSegment(sketch, "E360", {"start": v(-661, -263.85) * mm, "end": v(-661, -328.85) * mm});
            skLineSegment(sketch, "E361", {"start": v(-653.5, -263.85) * mm, "end": v(-653.5, -328.85) * mm});
            skLineSegment(sketch, "E362", {"start": v(-442, -328.85) * mm, "end": v(-442, -263.85) * mm});
            skLineSegment(sketch, "E363", {"start": v(-766.75, -253.85) * mm, "end": v(-872.5, -253.85) * mm});
            skLineSegment(sketch, "E364", {"start": v(-547.75, -253.85) * mm, "end": v(-759.25, -253.85) * mm});
            skLineSegment(sketch, "E365", {"start": v(-766.75, -188.85) * mm, "end": v(-872.5, -188.85) * mm});
            skLineSegment(sketch, "E366", {"start": v(-547.75, -188.85) * mm, "end": v(-759.25, -188.85) * mm});
            skLineSegment(sketch, "E367", {"start": v(-766.75, -188.85) * mm, "end": v(-766.75, -253.85) * mm});
            skLineSegment(sketch, "E368", {"start": v(-759.25, -188.85) * mm, "end": v(-759.25, -253.85) * mm});
            skLineSegment(sketch, "E369", {"start": v(-547.75, -253.85) * mm, "end": v(-547.75, -188.85) * mm});
            skLineSegment(sketch, "E370", {"start": v(-540.25, -253.85) * mm, "end": v(-540.25, -188.85) * mm});
            skLineSegment(sketch, "E371", {"start": v(-661, -478.85) * mm, "end": v(-872.5, -478.85) * mm});
            skLineSegment(sketch, "E372", {"start": v(-442, -478.85) * mm, "end": v(-653.5, -478.85) * mm});
            skLineSegment(sketch, "E373", {"start": v(-661, -413.85) * mm, "end": v(-872.5, -413.85) * mm});
            skLineSegment(sketch, "E374", {"start": v(-442, -413.85) * mm, "end": v(-653.5, -413.85) * mm});
            skLineSegment(sketch, "E375", {"start": v(-661, -413.85) * mm, "end": v(-661, -478.85) * mm});
            skLineSegment(sketch, "E376", {"start": v(-653.5, -413.85) * mm, "end": v(-653.5, -478.85) * mm});
            skLineSegment(sketch, "E377", {"start": v(-442, -478.85) * mm, "end": v(-442, -413.85) * mm});
            skLineSegment(sketch, "E378", {"start": v(-766.75, -403.85) * mm, "end": v(-872.5, -403.85) * mm});
            skLineSegment(sketch, "E379", {"start": v(-547.75, -403.85) * mm, "end": v(-759.25, -403.85) * mm});
            skLineSegment(sketch, "E380", {"start": v(-547.75, -338.85) * mm, "end": v(-759.25, -338.85) * mm});
            skLineSegment(sketch, "E381", {"start": v(-766.75, -338.85) * mm, "end": v(-766.75, -403.85) * mm});
            skLineSegment(sketch, "E382", {"start": v(-759.25, -338.85) * mm, "end": v(-759.25, -403.85) * mm});
            skLineSegment(sketch, "E383", {"start": v(-547.75, -403.85) * mm, "end": v(-547.75, -338.85) * mm});
            skLineSegment(sketch, "E384", {"start": v(-540.25, -403.85) * mm, "end": v(-540.25, -338.85) * mm});
            skLineSegment(sketch, "E385", {"start": v(-766.75, -338.85) * mm, "end": v(-872.5, -338.85) * mm});
            skLineSegment(sketch, "E386", {"start": v(-661, -628.85) * mm, "end": v(-872.5, -628.85) * mm});
            skLineSegment(sketch, "E387", {"start": v(-442, -628.85) * mm, "end": v(-653.5, -628.85) * mm});
            skLineSegment(sketch, "E388", {"start": v(-661, -563.85) * mm, "end": v(-872.5, -563.85) * mm});
            skLineSegment(sketch, "E389", {"start": v(-442, -563.85) * mm, "end": v(-653.5, -563.85) * mm});
            skLineSegment(sketch, "E390", {"start": v(-661, -563.85) * mm, "end": v(-661, -628.85) * mm});
            skLineSegment(sketch, "E391", {"start": v(-653.5, -563.85) * mm, "end": v(-653.5, -628.85) * mm});
            skLineSegment(sketch, "E392", {"start": v(-442, -628.85) * mm, "end": v(-442, -563.85) * mm});
            skLineSegment(sketch, "E393", {"start": v(-766.75, -553.85) * mm, "end": v(-872.5, -553.85) * mm});
            skLineSegment(sketch, "E394", {"start": v(-547.75, -553.85) * mm, "end": v(-759.25, -553.85) * mm});
            skLineSegment(sketch, "E395", {"start": v(-766.75, -488.85) * mm, "end": v(-872.5, -488.85) * mm});
            skLineSegment(sketch, "E396", {"start": v(-547.75, -488.85) * mm, "end": v(-759.25, -488.85) * mm});
            skLineSegment(sketch, "E397", {"start": v(-766.75, -488.85) * mm, "end": v(-766.75, -553.85) * mm});
            skLineSegment(sketch, "E398", {"start": v(-759.25, -488.85) * mm, "end": v(-759.25, -553.85) * mm});
            skLineSegment(sketch, "E399", {"start": v(-547.75, -553.85) * mm, "end": v(-547.75, -488.85) * mm});
            skLineSegment(sketch, "E400", {"start": v(-540.25, -553.85) * mm, "end": v(-540.25, -488.85) * mm});
            skLineSegment(sketch, "E401", {"start": v(-661, -713.85) * mm, "end": v(-872.5, -713.85) * mm});
            skLineSegment(sketch, "E402", {"start": v(-442, -713.85) * mm, "end": v(-653.5, -713.85) * mm});
            skLineSegment(sketch, "E403", {"start": v(-661, -713.85) * mm, "end": v(-661, -743.85) * mm});
            skLineSegment(sketch, "E404", {"start": v(-653.5, -713.85) * mm, "end": v(-653.5, -743.85) * mm});
            skLineSegment(sketch, "E405", {"start": v(-766.75, -703.85) * mm, "end": v(-872.5, -703.85) * mm});
            skLineSegment(sketch, "E406", {"start": v(-547.75, -703.85) * mm, "end": v(-759.25, -703.85) * mm});
            skLineSegment(sketch, "E407", {"start": v(-547.75, -638.85) * mm, "end": v(-759.25, -638.85) * mm});
            skLineSegment(sketch, "E408", {"start": v(-442, -628.85) * mm, "end": v(-540.25, -628.85) * mm});
            skLineSegment(sketch, "E409", {"start": v(-442, -563.85) * mm, "end": v(-540.25, -563.85) * mm});
            skLineSegment(sketch, "E410", {"start": v(-766.75, -638.85) * mm, "end": v(-766.75, -703.85) * mm});
            skLineSegment(sketch, "E411", {"start": v(-759.25, -638.85) * mm, "end": v(-759.25, -703.85) * mm});
            skLineSegment(sketch, "E412", {"start": v(-547.75, -703.85) * mm, "end": v(-547.75, -638.85) * mm});
            skLineSegment(sketch, "E413", {"start": v(-540.25, -703.85) * mm, "end": v(-540.25, -638.85) * mm});
            skLineSegment(sketch, "E414", {"start": v(-766.75, -638.85) * mm, "end": v(-872.5, -638.85) * mm});
            skLineSegment(sketch, "E415", {"start": v(-442, -713.85) * mm, "end": v(-540.25, -713.85) * mm});
            skLineSegment(sketch, "E416", {"start": v(441.5, -743.85) * mm, "end": v(441.5, 199.9) * mm});
            skLineSegment(sketch, "E417", {"start": v(-442, -743.85) * mm, "end": v(-442, 199.8) * mm});
            skLineSegment(sketch, "E418", {"start": v(-442, 111.15) * mm, "end": v(-540.25, 111.15) * mm});
            skLineSegment(sketch, "E419", {"start": v(-442, 46.15) * mm, "end": v(-540.25, 46.15) * mm});
            skLineSegment(sketch, "E420", {"start": v(-442, -38.85) * mm, "end": v(-540.25, -38.85) * mm});
            skLineSegment(sketch, "E421", {"start": v(-442, -103.85) * mm, "end": v(-540.25, -103.85) * mm});
            skLineSegment(sketch, "E422", {"start": v(-442, -188.85) * mm, "end": v(-540.25, -188.85) * mm});
            skLineSegment(sketch, "E423", {"start": v(-442, -253.85) * mm, "end": v(-540.25, -253.85) * mm});
            skLineSegment(sketch, "E424", {"start": v(-442, -338.85) * mm, "end": v(-540.25, -338.85) * mm});
            skLineSegment(sketch, "E425", {"start": v(-442, -403.85) * mm, "end": v(-540.25, -403.85) * mm});
            skLineSegment(sketch, "E426", {"start": v(546.75, 111.15) * mm, "end": v(441, 111.15) * mm});
            skLineSegment(sketch, "E427", {"start": v(546.75, 46.15) * mm, "end": v(441, 46.15) * mm});
            skLineSegment(sketch, "E428", {"start": v(-442, -553.85) * mm, "end": v(-540.25, -553.85) * mm});
            skLineSegment(sketch, "E429", {"start": v(-442, -488.85) * mm, "end": v(-540.25, -488.85) * mm});
            skLineSegment(sketch, "E430", {"start": v(-442, 199.8) * mm, "end": v(-483.39, 413.84) * mm});
            skLineSegment(sketch, "E431", {"start": v(482.84, 413.95) * mm, "end": v(441.5, 199.9) * mm});
            skLineSegment(sketch, "E432", {"start": v(-378, 211.26) * mm, "end": v(-397.57, 312.42) * mm});
            skLineSegment(sketch, "E433", {"start": v(-409.54, 427) * mm, "end": v(-392.97, 325.34) * mm});
            skLineSegment(sketch, "E434", {"start": v(-345.26, 436.63) * mm, "end": v(-328.68, 334.94) * mm});
            skLineSegment(sketch, "E435", {"start": v(-335.34, 437.97) * mm, "end": v(-321.78, 335.87) * mm});
            skLineSegment(sketch, "E436", {"start": v(-270.8, 445.7) * mm, "end": v(-257.23, 343.57) * mm});
            skLineSegment(sketch, "E437", {"start": v(-260.76, 446.76) * mm, "end": v(-250.21, 344.3) * mm});
            skLineSegment(sketch, "E438", {"start": v(-185.95, 453.35) * mm, "end": v(-178.43, 350.63) * mm});
            skLineSegment(sketch, "E439", {"start": v(-110.98, 457.73) * mm, "end": v(-106.5, 354.83) * mm});
            skLineSegment(sketch, "E440", {"start": v(-35.91, 459.9) * mm, "end": v(-34.46, 356.9) * mm});
            skLineSegment(sketch, "E441", {"start": v(39.18, 459.85) * mm, "end": v(37.6, 356.86) * mm});
            skLineSegment(sketch, "E442", {"start": v(114.25, 457.59) * mm, "end": v(109.62, 354.69) * mm});
            skLineSegment(sketch, "E443", {"start": v(189.21, 453.1) * mm, "end": v(181.56, 350.4) * mm});
            skLineSegment(sketch, "E444", {"start": v(-196.02, 452.6) * mm, "end": v(-185.46, 350.1) * mm});
            skLineSegment(sketch, "E445", {"start": v(-121.06, 457.27) * mm, "end": v(-113.54, 354.5) * mm});
            skLineSegment(sketch, "E446", {"start": v(-46, 459.73) * mm, "end": v(-41.52, 356.8) * mm});
            skLineSegment(sketch, "E447", {"start": v(29.1, 459.98) * mm, "end": v(30.54, 356.96) * mm});
            skLineSegment(sketch, "E448", {"start": v(104.16, 458.02) * mm, "end": v(102.58, 355) * mm});
            skLineSegment(sketch, "E449", {"start": v(179.14, 453.84) * mm, "end": v(174.52, 350.9) * mm});
            skLineSegment(sketch, "E450", {"start": v(253.97, 447.45) * mm, "end": v(246.31, 344.7) * mm});
            skLineSegment(sketch, "E451", {"start": v(264.01, 446.42) * mm, "end": v(253.33, 343.98) * mm});
            skLineSegment(sketch, "E452", {"start": v(338.58, 437.54) * mm, "end": v(324.88, 335.45) * mm});
            skLineSegment(sketch, "E453", {"start": v(328.57, 438.86) * mm, "end": v(317.9, 336.38) * mm});
            skArc(sketch, "E454", {"start": v(-399.85, 324.2) * mm, "mid": v(-431.88, 318.67) * mm, "end": v(-463.83, 312.72) * mm});
            skLineSegment(sketch, "E455", {"start": v(-399.85, 324.2) * mm, "end": v(-419.57, 426.18) * mm});
            skLineSegment(sketch, "E456", {"start": v(-391.04, 313.5) * mm, "end": v(-374.48, 211.83) * mm});
            skArc(sketch, "E457", {"start": v(-397.57, 312.42) * mm, "mid": v(-429.6, 306.9) * mm, "end": v(-461.55, 300.93) * mm});
            skArc(sketch, "E458", {"start": v(-326.75, 323.1) * mm, "mid": v(-358.93, 318.5) * mm, "end": v(-391.04, 313.5) * mm});
            skLineSegment(sketch, "E459", {"start": v(-326.75, 323.1) * mm, "end": v(-310.18, 221.4) * mm});
            skArc(sketch, "E460", {"start": v(-328.68, 334.94) * mm, "mid": v(-360.86, 330.35) * mm, "end": v(-392.97, 325.34) * mm});
            skLineSegment(sketch, "E461", {"start": v(-320.2, 323.97) * mm, "end": v(-306.63, 221.87) * mm});
            skArc(sketch, "E462", {"start": v(-255.65, 331.67) * mm, "mid": v(-287.95, 328.04) * mm, "end": v(-320.2, 323.97) * mm});
            skLineSegment(sketch, "E463", {"start": v(-255.65, 331.67) * mm, "end": v(-242.08, 229.53) * mm});
            skLineSegment(sketch, "E464", {"start": v(-248.98, 332.37) * mm, "end": v(-238.43, 229.9) * mm});
            skArc(sketch, "E465", {"start": v(-185.46, 350.1) * mm, "mid": v(-217.86, 347.42) * mm, "end": v(-250.21, 344.3) * mm});
            skLineSegment(sketch, "E466", {"start": v(-177.55, 338.66) * mm, "end": v(-170.03, 235.93) * mm});
            skLineSegment(sketch, "E467", {"start": v(-184.23, 338.16) * mm, "end": v(-173.68, 235.66) * mm});
            skArc(sketch, "E468", {"start": v(-184.23, 338.16) * mm, "mid": v(-216.63, 335.48) * mm, "end": v(-248.98, 332.37) * mm});
            skArc(sketch, "E469", {"start": v(-113.54, 354.5) * mm, "mid": v(-146, 352.78) * mm, "end": v(-178.43, 350.63) * mm});
            skLineSegment(sketch, "E470", {"start": v(-105.97, 342.84) * mm, "end": v(-101.48, 239.94) * mm});
            skLineSegment(sketch, "E471", {"start": v(-112.66, 342.54) * mm, "end": v(-105.14, 239.77) * mm});
            skArc(sketch, "E472", {"start": v(-112.66, 342.54) * mm, "mid": v(-145.12, 340.81) * mm, "end": v(-177.55, 338.66) * mm});
            skArc(sketch, "E473", {"start": v(-41.52, 356.8) * mm, "mid": v(-74.01, 356.03) * mm, "end": v(-106.5, 354.83) * mm});
            skLineSegment(sketch, "E474", {"start": v(-34.3, 344.9) * mm, "end": v(-32.84, 241.92) * mm});
            skLineSegment(sketch, "E475", {"start": v(-41, 344.8) * mm, "end": v(-36.5, 241.86) * mm});
            skArc(sketch, "E476", {"start": v(-41, 344.8) * mm, "mid": v(-73.49, 344.04) * mm, "end": v(-105.97, 342.84) * mm});
            skArc(sketch, "E477", {"start": v(30.54, 356.96) * mm, "mid": v(-1.96, 357.15) * mm, "end": v(-34.46, 356.9) * mm});
            skArc(sketch, "E478", {"start": v(30.71, 344.96) * mm, "mid": v(-1.8, 345.15) * mm, "end": v(-34.3, 344.9) * mm});
            skLineSegment(sketch, "E479", {"start": v(30.71, 344.96) * mm, "end": v(32.17, 241.93) * mm});
            skArc(sketch, "E480", {"start": v(102.58, 355) * mm, "mid": v(70.1, 356.14) * mm, "end": v(37.6, 356.86) * mm});
            skLineSegment(sketch, "E481", {"start": v(109.09, 342.7) * mm, "end": v(104.46, 239.8) * mm});
            skLineSegment(sketch, "E482", {"start": v(102.4, 343) * mm, "end": v(100.8, 239.97) * mm});
            skArc(sketch, "E483", {"start": v(102.4, 343) * mm, "mid": v(69.9, 344.14) * mm, "end": v(37.41, 344.86) * mm});
            skArc(sketch, "E484", {"start": v(174.52, 350.9) * mm, "mid": v(142.09, 353.01) * mm, "end": v(109.62, 354.69) * mm});
            skArc(sketch, "E485", {"start": v(173.98, 338.92) * mm, "mid": v(141.55, 341.03) * mm, "end": v(109.09, 342.7) * mm});
            skLineSegment(sketch, "E486", {"start": v(173.98, 338.92) * mm, "end": v(169.36, 235.98) * mm});
            skLineSegment(sketch, "E487", {"start": v(180.66, 338.43) * mm, "end": v(173.01, 235.71) * mm});
            skArc(sketch, "E488", {"start": v(246.31, 344.7) * mm, "mid": v(213.95, 347.76) * mm, "end": v(181.56, 350.4) * mm});
            skLineSegment(sketch, "E489", {"start": v(252.09, 332.04) * mm, "end": v(241.4, 229.6) * mm});
            skLineSegment(sketch, "E490", {"start": v(245.42, 332.73) * mm, "end": v(237.76, 229.98) * mm});
            skArc(sketch, "E491", {"start": v(245.42, 332.73) * mm, "mid": v(213.06, 335.8) * mm, "end": v(180.66, 338.43) * mm});
            skArc(sketch, "E492", {"start": v(317.9, 336.38) * mm, "mid": v(285.64, 340.4) * mm, "end": v(253.33, 343.98) * mm});
            skLineSegment(sketch, "E493", {"start": v(323.29, 323.56) * mm, "end": v(309.6, 221.47) * mm});
            skLineSegment(sketch, "E494", {"start": v(316.65, 324.44) * mm, "end": v(305.96, 221.96) * mm});
            skArc(sketch, "E495", {"start": v(387.6, 314.05) * mm, "mid": v(387.44, 314.08) * mm, "end": v(387.28, 314.1) * mm});
            skArc(sketch, "E496", {"start": v(389.2, 325.95) * mm, "mid": v(357.07, 330.92) * mm, "end": v(324.88, 335.45) * mm});
            skLineSegment(sketch, "E497", {"start": v(37.41, 344.86) * mm, "end": v(35.83, 241.87) * mm});
            skLineSegment(sketch, "E498", {"start": v(370.87, 212.42) * mm, "end": v(387.28, 314.1) * mm});
            skArc(sketch, "E499", {"start": v(387.28, 314.1) * mm, "mid": v(355.32, 319.04) * mm, "end": v(323.29, 323.56) * mm});
            skLineSegment(sketch, "E500", {"start": v(389.2, 325.95) * mm, "end": v(405.6, 427.64) * mm});
            skLineSegment(sketch, "E501", {"start": v(377.5, 211.34) * mm, "end": v(396.06, 312.67) * mm});
            skLineSegment(sketch, "E502", {"start": v(398.22, 324.48) * mm, "end": v(416.78, 425.8) * mm});
            skLineSegment(sketch, "E503", {"start": v(489.94, 411.15) * mm, "end": v(477.38, 346.15) * mm});
            skLineSegment(sketch, "E504", {"start": v(475.45, 336.15) * mm, "end": v(462.9, 271.15) * mm});
            skLineSegment(sketch, "E505", {"start": v(460.97, 261.15) * mm, "end": v(448.41, 196.15) * mm});
            skArc(sketch, "E506", {"start": v(485.1, 421.15) * mm, "mid": v(463.32, 425.27) * mm, "end": v(441.5, 429.2) * mm});
            skArc(sketch, "E507", {"start": v(-442, 429.1) * mm, "mid": v(-463.57, 425.22) * mm, "end": v(-485.1, 421.15) * mm});
            skArc(sketch, "E508", {"start": v(-223, 457.9) * mm, "mid": v(-329.04, 446.36) * mm, "end": v(-434.5, 430.41) * mm});
            skArc(sketch, "E509", {"start": v(-4, 467.65) * mm, "mid": v(-109.84, 465.29) * mm, "end": v(-215.5, 458.54) * mm});
            skArc(sketch, "E510", {"start": v(215, 458.58) * mm, "mid": v(109.34, 465.3) * mm, "end": v(3.5, 467.65) * mm});
            skArc(sketch, "E511", {"start": v(434, 430.5) * mm, "mid": v(328.54, 446.43) * mm, "end": v(222.5, 457.94) * mm});
            skLineSegment(sketch, "E512", {"start": v(872, 1043.85) * mm, "end": v(872, -743.85) * mm});
            skLineSegment(sketch, "E513", {"start": v(653, -28.85) * mm, "end": v(441.5, -28.85) * mm});
            skLineSegment(sketch, "E514", {"start": v(872, -28.85) * mm, "end": v(660.5, -28.85) * mm});
            skLineSegment(sketch, "E515", {"start": v(653, 36.15) * mm, "end": v(441.5, 36.15) * mm});
            skLineSegment(sketch, "E516", {"start": v(872, 36.15) * mm, "end": v(660.5, 36.15) * mm});
            skLineSegment(sketch, "E517", {"start": v(653, -28.85) * mm, "end": v(653, 36.15) * mm});
            skLineSegment(sketch, "E518", {"start": v(660.5, -28.85) * mm, "end": v(660.5, 36.15) * mm});
            skLineSegment(sketch, "E519", {"start": v(872, -28.85) * mm, "end": v(872, 36.15) * mm});
            skLineSegment(sketch, "E520", {"start": v(872, -38.85) * mm, "end": v(773.25, -38.85) * mm});
            skLineSegment(sketch, "E521", {"start": v(872, -103.85) * mm, "end": v(872, -38.85) * mm});
            skLineSegment(sketch, "E522", {"start": v(765.75, -103.85) * mm, "end": v(554.25, -103.85) * mm});
            skLineSegment(sketch, "E523", {"start": v(660.5, -38.85) * mm, "end": v(554.25, -38.85) * mm});
            skLineSegment(sketch, "E524", {"start": v(546.75, -103.85) * mm, "end": v(546.75, -38.85) * mm});
            skLineSegment(sketch, "E525", {"start": v(554.25, -103.85) * mm, "end": v(554.25, -38.85) * mm});
            skLineSegment(sketch, "E526", {"start": v(765.75, -103.85) * mm, "end": v(765.75, -38.85) * mm});
            skLineSegment(sketch, "E527", {"start": v(773.25, -103.85) * mm, "end": v(773.25, -38.85) * mm});
            skLineSegment(sketch, "E528", {"start": v(773.25, -38.85) * mm, "end": v(872, -38.85) * mm});
            skLineSegment(sketch, "E529", {"start": v(773.25, -103.85) * mm, "end": v(871.5, -103.85) * mm});
            skLineSegment(sketch, "E530", {"start": v(546.75, -38.85) * mm, "end": v(441, -38.85) * mm});
            skLineSegment(sketch, "E531", {"start": v(546.75, -103.85) * mm, "end": v(441, -103.85) * mm});
            skLineSegment(sketch, "E532", {"start": v(653, -178.85) * mm, "end": v(441.5, -178.85) * mm});
            skLineSegment(sketch, "E533", {"start": v(872, -178.85) * mm, "end": v(660.5, -178.85) * mm});
            skLineSegment(sketch, "E534", {"start": v(653, -113.85) * mm, "end": v(441.5, -113.85) * mm});
            skLineSegment(sketch, "E535", {"start": v(872, -113.85) * mm, "end": v(660.5, -113.85) * mm});
            skLineSegment(sketch, "E536", {"start": v(653, -178.85) * mm, "end": v(653, -113.85) * mm});
            skLineSegment(sketch, "E537", {"start": v(660.5, -178.85) * mm, "end": v(660.5, -113.85) * mm});
            skLineSegment(sketch, "E538", {"start": v(872, -178.85) * mm, "end": v(872, -113.85) * mm});
            skLineSegment(sketch, "E539", {"start": v(872, -188.85) * mm, "end": v(773.25, -188.85) * mm});
            skLineSegment(sketch, "E540", {"start": v(872, -253.85) * mm, "end": v(872, -188.85) * mm});
            skLineSegment(sketch, "E541", {"start": v(765.75, -253.85) * mm, "end": v(554.25, -253.85) * mm});
            skLineSegment(sketch, "E542", {"start": v(765.75, -188.85) * mm, "end": v(554.25, -188.85) * mm});
            skLineSegment(sketch, "E543", {"start": v(546.75, -253.85) * mm, "end": v(546.75, -188.85) * mm});
            skLineSegment(sketch, "E544", {"start": v(554.25, -253.85) * mm, "end": v(554.25, -188.85) * mm});
            skLineSegment(sketch, "E545", {"start": v(765.75, -253.85) * mm, "end": v(765.75, -188.85) * mm});
            skLineSegment(sketch, "E546", {"start": v(773.25, -253.85) * mm, "end": v(773.25, -188.85) * mm});
            skLineSegment(sketch, "E547", {"start": v(773.25, -188.85) * mm, "end": v(872, -188.85) * mm});
            skLineSegment(sketch, "E548", {"start": v(773.25, -253.85) * mm, "end": v(871.5, -253.85) * mm});
            skLineSegment(sketch, "E549", {"start": v(546.75, -188.85) * mm, "end": v(441, -188.85) * mm});
            skLineSegment(sketch, "E550", {"start": v(546.75, -253.85) * mm, "end": v(441, -253.85) * mm});
            skLineSegment(sketch, "E551", {"start": v(653, -328.85) * mm, "end": v(441.5, -328.85) * mm});
            skLineSegment(sketch, "E552", {"start": v(872, -328.85) * mm, "end": v(660.5, -328.85) * mm});
            skLineSegment(sketch, "E553", {"start": v(653, -263.85) * mm, "end": v(441.5, -263.85) * mm});
            skLineSegment(sketch, "E554", {"start": v(872, -263.85) * mm, "end": v(660.5, -263.85) * mm});
            skLineSegment(sketch, "E555", {"start": v(653, -328.85) * mm, "end": v(653, -263.85) * mm});
            skLineSegment(sketch, "E556", {"start": v(660.5, -328.85) * mm, "end": v(660.5, -263.85) * mm});
            skLineSegment(sketch, "E557", {"start": v(872, -328.85) * mm, "end": v(872, -263.85) * mm});
            skLineSegment(sketch, "E558", {"start": v(872, -338.85) * mm, "end": v(773.25, -338.85) * mm});
            skLineSegment(sketch, "E559", {"start": v(872, -403.85) * mm, "end": v(872, -338.85) * mm});
            skLineSegment(sketch, "E560", {"start": v(765.75, -403.85) * mm, "end": v(554.25, -403.85) * mm});
            skLineSegment(sketch, "E561", {"start": v(765.75, -338.85) * mm, "end": v(554.25, -338.85) * mm});
            skLineSegment(sketch, "E562", {"start": v(546.75, -403.85) * mm, "end": v(546.75, -338.85) * mm});
            skLineSegment(sketch, "E563", {"start": v(554.25, -403.85) * mm, "end": v(554.25, -338.85) * mm});
            skLineSegment(sketch, "E564", {"start": v(765.75, -403.85) * mm, "end": v(765.75, -338.85) * mm});
            skLineSegment(sketch, "E565", {"start": v(773.25, -403.85) * mm, "end": v(773.25, -338.85) * mm});
            skLineSegment(sketch, "E566", {"start": v(773.25, -338.85) * mm, "end": v(872, -338.85) * mm});
            skLineSegment(sketch, "E567", {"start": v(773.25, -403.85) * mm, "end": v(871.5, -403.85) * mm});
            skLineSegment(sketch, "E568", {"start": v(546.75, -338.85) * mm, "end": v(441, -338.85) * mm});
            skLineSegment(sketch, "E569", {"start": v(546.75, -403.85) * mm, "end": v(441, -403.85) * mm});
            skLineSegment(sketch, "E570", {"start": v(653, -478.85) * mm, "end": v(441.5, -478.85) * mm});
            skLineSegment(sketch, "E571", {"start": v(872, -478.85) * mm, "end": v(660.5, -478.85) * mm});
            skLineSegment(sketch, "E572", {"start": v(653, -413.85) * mm, "end": v(441.5, -413.85) * mm});
            skLineSegment(sketch, "E573", {"start": v(872, -413.85) * mm, "end": v(660.5, -413.85) * mm});
            skLineSegment(sketch, "E574", {"start": v(653, -478.85) * mm, "end": v(653, -413.85) * mm});
            skLineSegment(sketch, "E575", {"start": v(660.5, -478.85) * mm, "end": v(660.5, -413.85) * mm});
            skLineSegment(sketch, "E576", {"start": v(872, -478.85) * mm, "end": v(872, -413.85) * mm});
            skLineSegment(sketch, "E577", {"start": v(872, -488.85) * mm, "end": v(773.25, -488.85) * mm});
            skLineSegment(sketch, "E578", {"start": v(872, -553.85) * mm, "end": v(872, -488.85) * mm});
            skLineSegment(sketch, "E579", {"start": v(765.75, -553.85) * mm, "end": v(554.25, -553.85) * mm});
            skLineSegment(sketch, "E580", {"start": v(765.75, -488.85) * mm, "end": v(554.25, -488.85) * mm});
            skLineSegment(sketch, "E581", {"start": v(546.75, -553.85) * mm, "end": v(546.75, -488.85) * mm});
            skLineSegment(sketch, "E582", {"start": v(554.25, -553.85) * mm, "end": v(554.25, -488.85) * mm});
            skLineSegment(sketch, "E583", {"start": v(765.75, -553.85) * mm, "end": v(765.75, -488.85) * mm});
            skLineSegment(sketch, "E584", {"start": v(773.25, -553.85) * mm, "end": v(773.25, -488.85) * mm});
            skLineSegment(sketch, "E585", {"start": v(773.25, -488.85) * mm, "end": v(872, -488.85) * mm});
            skLineSegment(sketch, "E586", {"start": v(773.25, -553.85) * mm, "end": v(871.5, -553.85) * mm});
            skLineSegment(sketch, "E587", {"start": v(546.75, -488.85) * mm, "end": v(441.5, -488.85) * mm});
            skLineSegment(sketch, "E588", {"start": v(546.75, -553.85) * mm, "end": v(441.5, -553.85) * mm});
            skLineSegment(sketch, "E589", {"start": v(653, -628.85) * mm, "end": v(441.5, -628.85) * mm});
            skLineSegment(sketch, "E590", {"start": v(872, -628.85) * mm, "end": v(660.5, -628.85) * mm});
            skLineSegment(sketch, "E591", {"start": v(653, -563.85) * mm, "end": v(441.5, -563.85) * mm});
            skLineSegment(sketch, "E592", {"start": v(872, -563.85) * mm, "end": v(660.5, -563.85) * mm});
            skLineSegment(sketch, "E593", {"start": v(653, -628.85) * mm, "end": v(653, -563.85) * mm});
            skLineSegment(sketch, "E594", {"start": v(660.5, -628.85) * mm, "end": v(660.5, -563.85) * mm});
            skLineSegment(sketch, "E595", {"start": v(872, -628.85) * mm, "end": v(872, -563.85) * mm});
            skLineSegment(sketch, "E596", {"start": v(872, -638.85) * mm, "end": v(773.25, -638.85) * mm});
            skLineSegment(sketch, "E597", {"start": v(872, -703.85) * mm, "end": v(872, -638.85) * mm});
            skLineSegment(sketch, "E598", {"start": v(765.75, -703.85) * mm, "end": v(554.25, -703.85) * mm});
            skLineSegment(sketch, "E599", {"start": v(765.75, -638.85) * mm, "end": v(554.25, -638.85) * mm});
            skLineSegment(sketch, "E600", {"start": v(546.75, -703.85) * mm, "end": v(546.75, -638.85) * mm});
            skLineSegment(sketch, "E601", {"start": v(554.25, -703.85) * mm, "end": v(554.25, -638.85) * mm});
            skLineSegment(sketch, "E602", {"start": v(765.75, -703.85) * mm, "end": v(765.75, -638.85) * mm});
            skLineSegment(sketch, "E603", {"start": v(773.25, -703.85) * mm, "end": v(773.25, -638.85) * mm});
            skLineSegment(sketch, "E604", {"start": v(773.25, -638.85) * mm, "end": v(872, -638.85) * mm});
            skLineSegment(sketch, "E605", {"start": v(773.25, -703.85) * mm, "end": v(871.5, -703.85) * mm});
            skLineSegment(sketch, "E606", {"start": v(546.75, -638.85) * mm, "end": v(441, -638.85) * mm});
            skLineSegment(sketch, "E607", {"start": v(546.75, -703.85) * mm, "end": v(441, -703.85) * mm});
            skLineSegment(sketch, "E608", {"start": v(653, -713.85) * mm, "end": v(441.5, -713.85) * mm});
            skLineSegment(sketch, "E609", {"start": v(872, -713.85) * mm, "end": v(660.5, -713.85) * mm});
            skLineSegment(sketch, "E610", {"start": v(653, -743.85) * mm, "end": v(653, -713.85) * mm});
            skLineSegment(sketch, "E611", {"start": v(660.5, -743.85) * mm, "end": v(660.5, -713.85) * mm});
            skLineSegment(sketch, "E612", {"start": v(872, -743.85) * mm, "end": v(872, -713.85) * mm});
            skLineSegment(sketch, "E613", {"start": v(-540.25, -638.85) * mm, "end": v(-442, -638.85) * mm});
            skLineSegment(sketch, "E614", {"start": v(-540.25, -703.85) * mm, "end": v(-442, -703.85) * mm});
            skLineSegment(sketch, "E615", {"start": v(-547.75, 571.15) * mm, "end": v(554.75, 571.15) * mm});
            skLineSegment(sketch, "E616", {"start": v(-547.75, 486.15) * mm, "end": v(-547.75, 571.15) * mm});
            skLineSegment(sketch, "E617", {"start": v(-547.75, 486.15) * mm, "end": v(554.75, 486.15) * mm});
            skLineSegment(sketch, "E618", {"start": v(554.75, 486.15) * mm, "end": v(554.75, 571.15) * mm});
            skLineSegment(sketch, "E619", {"start": v(-442, -671.85) * mm, "end": v(441.5, -671.85) * mm});
            skLineSegment(sketch, "E620", {"start": v(-221.82, -736.46) * mm, "end": v(-433.32, -736.46) * mm});
            skLineSegment(sketch, "E621", {"start": v(-2.82, -736.46) * mm, "end": v(-214.32, -736.46) * mm});
            skLineSegment(sketch, "E622", {"start": v(-221.82, -671.85) * mm, "end": v(-221.82, -736.46) * mm});
            skLineSegment(sketch, "E623", {"start": v(-214.32, -671.85) * mm, "end": v(-214.32, -736.46) * mm});
            skLineSegment(sketch, "E624", {"start": v(-2.82, -736.46) * mm, "end": v(-2.82, -671.85) * mm});
            skLineSegment(sketch, "E625", {"start": v(-103.25, -743.85) * mm, "end": v(-314.75, -743.85) * mm});
            skLineSegment(sketch, "E626", {"start": v(-2.82, -736.46) * mm, "end": v(-101.07, -736.46) * mm});
            skLineSegment(sketch, "E627", {"start": v(-322.25, -743.85) * mm, "end": v(-428, -743.85) * mm});
            skLineSegment(sketch, "E628", {"start": v(-95.75, -743.85) * mm, "end": v(2.5, -743.85) * mm});
            skLineSegment(sketch, "E629", {"start": v(-433.32, -736.46) * mm, "end": v(-433.32, -671.85) * mm});
            skLineSegment(sketch, "E630", {"start": v(-221.82, -736.46) * mm, "end": v(-221.82, -671.85) * mm});
            skLineSegment(sketch, "E631", {"start": v(-214.32, -736.46) * mm, "end": v(-214.32, -671.85) * mm});
            skLineSegment(sketch, "E632", {"start": v(4.68, -736.46) * mm, "end": v(4.68, -671.85) * mm});
            skLineSegment(sketch, "E633", {"start": v(216.18, -736.46) * mm, "end": v(4.68, -736.46) * mm});
            skLineSegment(sketch, "E634", {"start": v(435.18, -736.46) * mm, "end": v(223.68, -736.46) * mm});
            skLineSegment(sketch, "E635", {"start": v(216.18, -671.85) * mm, "end": v(216.18, -736.46) * mm});
            skLineSegment(sketch, "E636", {"start": v(223.68, -671.85) * mm, "end": v(223.68, -736.46) * mm});
            skLineSegment(sketch, "E637", {"start": v(435.18, -736.46) * mm, "end": v(435.18, -671.85) * mm});
            skLineSegment(sketch, "E638", {"start": v(-442, -653.85) * mm, "end": v(441.5, -653.85) * mm});
            skLineSegment(sketch, "E639.trimOffspring", {"start": v(765.75, -638.85) * mm, "end": v(660.5, -638.85) * mm});
            skLineSegment(sketch, "E640.trimOffspring", {"start": v(765.75, -488.85) * mm, "end": v(660.5, -488.85) * mm});
            skLineSegment(sketch, "E641.trimOffspring", {"start": v(765.75, -338.85) * mm, "end": v(660.5, -338.85) * mm});
            skLineSegment(sketch, "E642.trimOffspring", {"start": v(765.75, -188.85) * mm, "end": v(660.5, -188.85) * mm});
            skLineSegment(sketch, "E643", {"start": v(660.5, -38.85) * mm, "end": v(765.75, -38.85) * mm});
            skLineSegment(sketch, "E644", {"start": v(872, -38.85) * mm, "end": v(872, -103.85) * mm});
            skLineSegment(sketch, "E645", {"start": v(871.5, -103.85) * mm, "end": v(872, -103.85) * mm});
            skLineSegment(sketch, "E646", {"start": v(871.5, 46.15) * mm, "end": v(872, 46.15) * mm});
            skLineSegment(sketch, "E647", {"start": v(871.5, -253.85) * mm, "end": v(872, -253.85) * mm});
            skLineSegment(sketch, "E648", {"start": v(871.5, -403.85) * mm, "end": v(872, -403.85) * mm});
            skLineSegment(sketch, "E649", {"start": v(871.5, -553.85) * mm, "end": v(872, -553.85) * mm});
            skLineSegment(sketch, "E650", {"start": v(871.5, -703.85) * mm, "end": v(872, -703.85) * mm});
            skLineSegment(sketch, "E651.trimOffspring", {"start": v(765.75, 111.15) * mm, "end": v(660.5, 111.15) * mm});
            skLineSegment(sketch, "E652", {"start": v(482.84, 413.95) * mm, "end": v(416.78, 425.8) * mm});
            skLineSegment(sketch, "E653", {"start": v(405.6, 427.64) * mm, "end": v(338.58, 437.54) * mm});
            skLineSegment(sketch, "E654", {"start": v(328.57, 438.86) * mm, "end": v(264.01, 446.42) * mm});
            skLineSegment(sketch, "E655", {"start": v(253.97, 447.45) * mm, "end": v(189.21, 453.1) * mm});
            skLineSegment(sketch, "E656", {"start": v(179.14, 453.84) * mm, "end": v(114.25, 457.59) * mm});
            skLineSegment(sketch, "E657", {"start": v(104.16, 458.02) * mm, "end": v(39.18, 459.85) * mm});
            skLineSegment(sketch, "E658", {"start": v(29.1, 459.98) * mm, "end": v(-35.91, 459.9) * mm});
            skLineSegment(sketch, "E659", {"start": v(-270.8, 445.7) * mm, "end": v(-335.34, 437.97) * mm});
            skLineSegment(sketch, "E660", {"start": v(-345.26, 436.63) * mm, "end": v(-409.54, 427) * mm});
            skLineSegment(sketch, "E661", {"start": v(-419.57, 426.18) * mm, "end": v(-483.39, 413.84) * mm});
            skLineSegment(sketch, "E662", {"start": v(-260.76, 446.76) * mm, "end": v(-196.02, 452.6) * mm});
            skLineSegment(sketch, "E663", {"start": v(-185.95, 453.35) * mm, "end": v(-121.06, 457.27) * mm});
            skLineSegment(sketch, "E664", {"start": v(-110.98, 457.73) * mm, "end": v(-46, 459.73) * mm});
            skLineSegment(sketch, "E665.0", {"start": v(-446.9, 198.86) * mm, "end": v(-458.95, 261.15) * mm});
            skLineSegment(sketch, "E666.trimOffspring", {"start": v(-475.4, 346.15) * mm, "end": v(-487.96, 411.15) * mm});
            skLineSegment(sketch, "E667.trimOffspring", {"start": v(-460.89, 271.15) * mm, "end": v(-473.46, 336.15) * mm});
            skLineSegment(sketch, "E668", {"start": v(-446.9, 198.86) * mm, "end": v(-446.39, 196.15) * mm});
            skLineSegment(sketch, "E669", {"start": v(-872.5, 1043.85) * mm, "end": v(872, 1043.85) * mm});
            skSolve(sketch);
        }
        {
            var Q0;
            {var subQ0=sQuery(id+"F0.wireOp",EDGE,"E30");Q0=makeQuery(id+"F0.imprint","IMPRINT",FACE,{"disambiguationData":[TD([[makeQuery(id+"F0.imprint","IMPRINT",EDGE,{"derivedFrom":subQ0}),-1.0]])]});}
            var Q1;
            Q1=makeQuery(id+"F0.imprint","IMPRINT",FACE,{"disambiguationData":[TD([[makeQuery(id+"F0.imprint","IMPRINT",EDGE,{"derivedFrom":sQuery(id+"F0.wireOp",EDGE,"E31")}),-1.0]])]});
            var Q2;
            Q2=makeQuery(id+"F0.imprint","IMPRINT",FACE,{"disambiguationData":[TD([[makeQuery(id+"F0.imprint","IMPRINT",EDGE,{"derivedFrom":sQuery(id+"F0.wireOp",EDGE,"E34")}),-1.0]])]});
            var Q3;
            Q3=makeQuery(id+"F0.imprint","IMPRINT",FACE,{"disambiguationData":[TD([[makeQuery(id+"F0.imprint","IMPRINT",EDGE,{"derivedFrom":sQuery(id+"F0.wireOp",EDGE,"E35")}),-1.0]])]});
            var Q4;
            Q4=makeQuery(id+"F0.imprint","IMPRINT",FACE,{"disambiguationData":[TD([[makeQuery(id+"F0.imprint","IMPRINT",EDGE,{"derivedFrom":sQuery(id+"F0.wireOp",EDGE,"E45")}),-1.0]])]});
            var Q5;
            Q5=makeQuery(id+"F0.imprint","IMPRINT",FACE,{"disambiguationData":[TD([[makeQuery(id+"F0.imprint","IMPRINT",EDGE,{"derivedFrom":sQuery(id+"F0.wireOp",EDGE,"E93")}),-1.0]])]});
            var Q6;
            Q6=makeQuery(id+"F0.imprint","IMPRINT",FACE,{"disambiguationData":[TD([[makeQuery(id+"F0.imprint","IMPRINT",EDGE,{"derivedFrom":sQuery(id+"F0.wireOp",EDGE,"E96")}),-1.0]])]});
            var Q7;
            Q7=makeQuery(id+"F0.imprint","IMPRINT",FACE,{"disambiguationData":[TD([[makeQuery(id+"F0.imprint","IMPRINT",EDGE,{"derivedFrom":sQuery(id+"F0.wireOp",EDGE,"E97")}),-1.0]])]});
            var Q8;
            Q8=makeQuery(id+"F0.imprint","IMPRINT",FACE,{"disambiguationData":[TD([[makeQuery(id+"F0.imprint","IMPRINT",EDGE,{"derivedFrom":sQuery(id+"F0.wireOp",EDGE,"E107")}),-1.0]])]});
            var Q9;
            {var subQ0=sQuery(id+"F0.wireOp",EDGE,"E82");Q9=makeQuery(id+"F0.imprint","IMPRINT",FACE,{"disambiguationData":[TD([[makeQuery(id+"F0.imprint","IMPRINT",EDGE,{"derivedFrom":subQ0}),-1.0]])]});}
            var Q10;
            {var subQ0=sQuery(id+"F0.wireOp",EDGE,"E14");Q10=makeQuery(id+"F0.imprint","IMPRINT",FACE,{"disambiguationData":[TD([[makeQuery(id+"F0.imprint","IMPRINT",EDGE,{"derivedFrom":subQ0}),-1.0]])]});}
            var Q11;
            {var subQ0=sQuery(id+"F0.wireOp",EDGE,"E62");Q11=makeQuery(id+"F0.imprint","IMPRINT",FACE,{"disambiguationData":[TD([[makeQuery(id+"F0.imprint","IMPRINT",EDGE,{"derivedFrom":subQ0}),-1.0]])]});}
            var Q12;
            {var subQ0=sQuery(id+"F0.wireOp",EDGE,"E46");Q12=makeQuery(id+"F0.imprint","IMPRINT",FACE,{"disambiguationData":[TD([[makeQuery(id+"F0.imprint","IMPRINT",EDGE,{"derivedFrom":subQ0}),-1.0]])]});}
            var Q13;
            Q13=makeQuery(id+"F0.imprint","IMPRINT",FACE,{"disambiguationData":[TD([[makeQuery(id+"F0.imprint","IMPRINT",EDGE,{"derivedFrom":sQuery(id+"F0.wireOp",EDGE,"E63")}),-1.0]])]});
            var Q14;
            Q14=makeQuery(id+"F0.imprint","IMPRINT",FACE,{"disambiguationData":[TD([[makeQuery(id+"F0.imprint","IMPRINT",EDGE,{"derivedFrom":sQuery(id+"F0.wireOp",EDGE,"E15")}),-1.0]])]});
            var Q15;
            Q15=makeQuery(id+"F0.imprint","IMPRINT",FACE,{"disambiguationData":[TD([[makeQuery(id+"F0.imprint","IMPRINT",EDGE,{"derivedFrom":sQuery(id+"F0.wireOp",EDGE,"E18")}),-1.0]])]});
            var Q16;
            Q16=makeQuery(id+"F0.imprint","IMPRINT",FACE,{"disambiguationData":[TD([[makeQuery(id+"F0.imprint","IMPRINT",EDGE,{"derivedFrom":sQuery(id+"F0.wireOp",EDGE,"E65")}),-1.0]])]});
            var Q17;
            Q17=makeQuery(id+"F0.imprint","IMPRINT",FACE,{"disambiguationData":[TD([[makeQuery(id+"F0.imprint","IMPRINT",EDGE,{"derivedFrom":sQuery(id+"F0.wireOp",EDGE,"E47")}),-1.0]])]});
            var Q18;
            Q18=makeQuery(id+"F0.imprint","IMPRINT",FACE,{"disambiguationData":[TD([[makeQuery(id+"F0.imprint","IMPRINT",EDGE,{"derivedFrom":sQuery(id+"F0.wireOp",EDGE,"E50")}),-1.0]])]});
            var Q19;
            Q19=makeQuery(id+"F0.imprint","IMPRINT",FACE,{"disambiguationData":[TD([[makeQuery(id+"F0.imprint","IMPRINT",EDGE,{"derivedFrom":sQuery(id+"F0.wireOp",EDGE,"E66")}),-1.0]])]});
            var Q20;
            Q20=makeQuery(id+"F0.imprint","IMPRINT",FACE,{"disambiguationData":[TD([[makeQuery(id+"F0.imprint","IMPRINT",EDGE,{"derivedFrom":sQuery(id+"F0.wireOp",EDGE,"E19")}),-1.0]])]});
            var Q21;
            {var subQ1=sQuery(id+"F0.wireOp",EDGE,"E76");Q21=makeQuery(id+"F0.imprint","IMPRINT",FACE,{"disambiguationData":[TD([[makeQuery(id+"F0.imprint","IMPRINT",EDGE,{"derivedFrom":subQ1}),-1.0]])]});}
            var Q22;
            Q22=makeQuery(id+"F0.imprint","IMPRINT",FACE,{"disambiguationData":[TD([[makeQuery(id+"F0.imprint","IMPRINT",EDGE,{"derivedFrom":sQuery(id+"F0.wireOp",EDGE,"E51")}),-1.0]])]});
            var Q23;
            Q23=makeQuery(id+"F0.imprint","IMPRINT",FACE,{"disambiguationData":[TD([[makeQuery(id+"F0.imprint","IMPRINT",EDGE,{"derivedFrom":sQuery(id+"F0.wireOp",EDGE,"E29")}),-1.0]])]});
            var Q24;
            Q24=makeQuery(id+"F0.imprint","IMPRINT",FACE,{"disambiguationData":[TD([[makeQuery(id+"F0.imprint","IMPRINT",EDGE,{"derivedFrom":sQuery(id+"F0.wireOp",EDGE,"E125")}),-1.0]])]});
            var Q25;
            Q25=makeQuery(id+"F0.imprint","IMPRINT",FACE,{"disambiguationData":[TD([[makeQuery(id+"F0.imprint","IMPRINT",EDGE,{"derivedFrom":sQuery(id+"F0.wireOp",EDGE,"E78")}),-1.0]])]});
            var Q26;
            Q26=makeQuery(id+"F0.imprint","IMPRINT",FACE,{"disambiguationData":[TD([[makeQuery(id+"F0.imprint","IMPRINT",EDGE,{"derivedFrom":sQuery(id+"F0.wireOp",EDGE,"E128")}),-1.0]])]});
            var Q27;
            Q27=makeQuery(id+"F0.imprint","IMPRINT",FACE,{"disambiguationData":[TD([[makeQuery(id+"F0.imprint","IMPRINT",EDGE,{"derivedFrom":sQuery(id+"F0.wireOp",EDGE,"E110")}),-1.0]])]});
            var Q28;
            Q28=makeQuery(id+"F0.imprint","IMPRINT",FACE,{"disambiguationData":[TD([[makeQuery(id+"F0.imprint","IMPRINT",EDGE,{"derivedFrom":sQuery(id+"F0.wireOp",EDGE,"E113")}),-1.0]])]});
            var Q29;
            {var subQ0=sQuery(id+"F0.wireOp",EDGE,"E139");Q29=makeQuery(id+"F0.imprint","IMPRINT",FACE,{"disambiguationData":[TD([[makeQuery(id+"F0.imprint","IMPRINT",EDGE,{"derivedFrom":subQ0}),-1.0]])]});}
            var Q30;
            {var subQ0=sQuery(id+"F0.wireOp",EDGE,"E114");Q30=makeQuery(id+"F0.imprint","IMPRINT",FACE,{"disambiguationData":[TD([[makeQuery(id+"F0.imprint","IMPRINT",EDGE,{"derivedFrom":subQ0}),-1.0]])]});}
            var Q31;
            Q31=makeQuery(id+"F0.imprint","IMPRINT",FACE,{"disambiguationData":[TD([[makeQuery(id+"F0.imprint","IMPRINT",EDGE,{"derivedFrom":sQuery(id+"F0.wireOp",EDGE,"E81")}),-1.0]])]});
            var Q32;
            Q32=makeQuery(id+"F0.imprint","IMPRINT",FACE,{"disambiguationData":[TD([[makeQuery(id+"F0.imprint","IMPRINT",EDGE,{"derivedFrom":sQuery(id+"F0.wireOp",EDGE,"E129")}),-1.0]])]});
            var Q33;
            Q33=makeQuery(id+"F0.imprint","IMPRINT",FACE,{"disambiguationData":[TD([[makeQuery(id+"F0.imprint","IMPRINT",EDGE,{"derivedFrom":sQuery(id+"F0.wireOp",EDGE,"E61")}),-1.0]])]});
            var Q34;
            {var subQ0=sQuery(id+"F0.wireOp",EDGE,"E161");Q34=makeQuery(id+"F0.imprint","IMPRINT",FACE,{"disambiguationData":[TD([[makeQuery(id+"F0.imprint","IMPRINT",EDGE,{"derivedFrom":subQ0}),-1.0]])]});}
            var Q35;
            {var subQ0=sQuery(id+"F0.wireOp",EDGE,"E145");Q35=makeQuery(id+"F0.imprint","IMPRINT",FACE,{"disambiguationData":[TD([[makeQuery(id+"F0.imprint","IMPRINT",EDGE,{"derivedFrom":subQ0}),-1.0]])]});}
            var Q36;
            {var subQ0=sQuery(id+"F0.wireOp",EDGE,"E191");Q36=makeQuery(id+"F0.imprint","IMPRINT",FACE,{"disambiguationData":[TD([[makeQuery(id+"F0.imprint","IMPRINT",EDGE,{"derivedFrom":subQ0}),-1.0]])]});}
            var Q37;
            {var subQ0=sQuery(id+"F0.wireOp",EDGE,"E192");Q37=makeQuery(id+"F0.imprint","IMPRINT",FACE,{"disambiguationData":[TD([[makeQuery(id+"F0.imprint","IMPRINT",EDGE,{"derivedFrom":subQ0}),-1.0]])]});}
            var Q38;
            Q38=makeQuery(id+"F0.imprint","IMPRINT",FACE,{"disambiguationData":[TD([[makeQuery(id+"F0.imprint","IMPRINT",EDGE,{"derivedFrom":sQuery(id+"F0.wireOp",EDGE,"E162")}),-1.0]])]});
            var Q39;
            {var subQ2=sQuery(id+"F0.wireOp",EDGE,"E146");Q39=makeQuery(id+"F0.imprint","IMPRINT",FACE,{"disambiguationData":[TD([[makeQuery(id+"F0.imprint","IMPRINT",EDGE,{"derivedFrom":subQ2}),-1.0]])]});}
            var Q40;
            Q40=makeQuery(id+"F0.imprint","IMPRINT",FACE,{"disambiguationData":[TD([[makeQuery(id+"F0.imprint","IMPRINT",EDGE,{"derivedFrom":sQuery(id+"F0.wireOp",EDGE,"E165")}),-1.0]])]});
            var Q41;
            Q41=makeQuery(id+"F0.imprint","IMPRINT",FACE,{"disambiguationData":[TD([[makeQuery(id+"F0.imprint","IMPRINT",EDGE,{"derivedFrom":sQuery(id+"F0.wireOp",EDGE,"E151")}),1.0]])]});
            var Q42;
            Q42=makeQuery(id+"F0.imprint","IMPRINT",FACE,{"disambiguationData":[TD([[makeQuery(id+"F0.imprint","IMPRINT",EDGE,{"derivedFrom":sQuery(id+"F0.wireOp",EDGE,"E166")}),-1.0]])]});
            var Q43;
            Q43=makeQuery(id+"F0.imprint","IMPRINT",FACE,{"disambiguationData":[TD([[makeQuery(id+"F0.imprint","IMPRINT",EDGE,{"derivedFrom":sQuery(id+"F0.wireOp",EDGE,"E152")}),1.0]])]});
            var Q44;
            Q44=makeQuery(id+"F0.imprint","IMPRINT",FACE,{"disambiguationData":[TD([[makeQuery(id+"F0.imprint","IMPRINT",EDGE,{"derivedFrom":sQuery(id+"F0.wireOp",EDGE,"E176")}),-1.0]])]});
            var Q45;
            {var subQ0=sQuery(id+"F0.wireOp",EDGE,"E160");Q45=makeQuery(id+"F0.imprint","IMPRINT",FACE,{"disambiguationData":[TD([[makeQuery(id+"F0.imprint","IMPRINT",EDGE,{"derivedFrom":subQ0}),-1.0]])]});}
            var Q46;
            Q46=makeQuery(id+"F0.imprint","IMPRINT",FACE,{"disambiguationData":[TD([[makeQuery(id+"F0.imprint","IMPRINT",EDGE,{"derivedFrom":sQuery(id+"F0.wireOp",EDGE,"E213")}),-1.0]])]});
            var Q47;
            Q47=makeQuery(id+"F0.imprint","IMPRINT",FACE,{"disambiguationData":[TD([[makeQuery(id+"F0.imprint","IMPRINT",EDGE,{"derivedFrom":sQuery(id+"F0.wireOp",EDGE,"E200")}),1.0]])]});
            var Q48;
            Q48=makeQuery(id+"F0.imprint","IMPRINT",FACE,{"disambiguationData":[TD([[makeQuery(id+"F0.imprint","IMPRINT",EDGE,{"derivedFrom":sQuery(id+"F0.wireOp",EDGE,"E216")}),-1.0]])]});
            var Q49;
            {var subQ1=sQuery(id+"F0.wireOp",EDGE,"E201");Q49=makeQuery(id+"F0.imprint","IMPRINT",FACE,{"disambiguationData":[TD([[makeQuery(id+"F0.imprint","IMPRINT",EDGE,{"derivedFrom":subQ1}),-1.0]])]});}
            var Q50;
            Q50=makeQuery(id+"F0.imprint","IMPRINT",FACE,{"disambiguationData":[TD([[makeQuery(id+"F0.imprint","IMPRINT",EDGE,{"derivedFrom":sQuery(id+"F0.wireOp",EDGE,"E217")}),-1.0]])]});
            var Q51;
            {var subQ0=sQuery(id+"F0.wireOp",EDGE,"E202");Q51=makeQuery(id+"F0.imprint","IMPRINT",FACE,{"disambiguationData":[TD([[makeQuery(id+"F0.imprint","IMPRINT",EDGE,{"derivedFrom":subQ0}),-1.0]])]});}
            var Q52;
            Q52=makeQuery(id+"F0.imprint","IMPRINT",FACE,{"disambiguationData":[TD([[makeQuery(id+"F0.imprint","IMPRINT",EDGE,{"derivedFrom":sQuery(id+"F0.wireOp",EDGE,"E227")}),-1.0]])]});
            var Q53;
            {var subQ0=sQuery(id+"F0.wireOp",EDGE,"E245");Q53=makeQuery(id+"F0.imprint","IMPRINT",FACE,{"disambiguationData":[TD([[makeQuery(id+"F0.imprint","IMPRINT",EDGE,{"derivedFrom":subQ0}),-1.0]])]});}
            var Q54;
            {var subQ0=sQuery(id+"F0.wireOp",EDGE,"E241");Q54=makeQuery(id+"F0.imprint","IMPRINT",FACE,{"disambiguationData":[TD([[makeQuery(id+"F0.imprint","IMPRINT",EDGE,{"derivedFrom":subQ0}),-1.0]])]});}
            var Q55;
            {var subQ0=sQuery(id+"F0.wireOp",EDGE,"E231");Q55=makeQuery(id+"F0.imprint","IMPRINT",FACE,{"disambiguationData":[TD([[makeQuery(id+"F0.imprint","IMPRINT",EDGE,{"derivedFrom":subQ0}),-1.0]])]});}
            var Q56;
            Q56=makeQuery(id+"F0.imprint","IMPRINT",FACE,{"disambiguationData":[TD([[makeQuery(id+"F0.imprint","IMPRINT",EDGE,{"derivedFrom":sQuery(id+"F0.wireOp",EDGE,"E230")}),-1.0]])]});
            var Q57;
            {var subQ0=sQuery(id+"F0.wireOp",EDGE,"E235");Q57=makeQuery(id+"F0.imprint","IMPRINT",FACE,{"disambiguationData":[TD([[makeQuery(id+"F0.imprint","IMPRINT",EDGE,{"derivedFrom":subQ0}),1.0]])]});}
            var Q58;
            {var subQ0=sQuery(id+"F0.wireOp",EDGE,"E190");Q58=makeQuery(id+"F0.imprint","IMPRINT",FACE,{"disambiguationData":[TD([[makeQuery(id+"F0.imprint","IMPRINT",EDGE,{"derivedFrom":subQ0}),-1.0]])]});}
            var Q59;
            {var subQ0=sQuery(id+"F0.wireOp",EDGE,"E188");Q59=makeQuery(id+"F0.imprint","IMPRINT",FACE,{"disambiguationData":[TD([[makeQuery(id+"F0.imprint","IMPRINT",EDGE,{"derivedFrom":subQ0}),-1.0]])]});}
            var Q60;
            {var subQ0=sQuery(id+"F0.wireOp",EDGE,"E186");Q60=makeQuery(id+"F0.imprint","IMPRINT",FACE,{"disambiguationData":[TD([[makeQuery(id+"F0.imprint","IMPRINT",EDGE,{"derivedFrom":subQ0}),-1.0]])]});}
            var Q61;
            Q61=makeQuery(id+"F0.imprint","IMPRINT",FACE,{"disambiguationData":[TD([[makeQuery(id+"F0.imprint","IMPRINT",EDGE,{"derivedFrom":sQuery(id+"F0.wireOp",EDGE,"E178")}),-1.0]])]});
            var Q62;
            {var subQ0=sQuery(id+"F0.wireOp",EDGE,"E177");Q62=makeQuery(id+"F0.imprint","IMPRINT",FACE,{"disambiguationData":[TD([[makeQuery(id+"F0.imprint","IMPRINT",EDGE,{"derivedFrom":subQ0}),-1.0]])]});}
            var Q63;
            {var subQ0=sQuery(id+"F0.wireOp",EDGE,"E257");Q63=makeQuery(id+"F0.imprint","IMPRINT",FACE,{"disambiguationData":[TD([[makeQuery(id+"F0.imprint","IMPRINT",EDGE,{"derivedFrom":subQ0}),-1.0]])]});}
            var Q64;
            Q64=makeQuery(id+"F0.imprint","IMPRINT",FACE,{"disambiguationData":[TD([[makeQuery(id+"F0.imprint","IMPRINT",EDGE,{"derivedFrom":sQuery(id+"F0.wireOp",EDGE,"E258")}),-1.0]])]});
            var Q65;
            Q65=makeQuery(id+"F0.imprint","IMPRINT",FACE,{"disambiguationData":[TD([[makeQuery(id+"F0.imprint","IMPRINT",EDGE,{"derivedFrom":sQuery(id+"F0.wireOp",EDGE,"E261")}),-1.0]])]});
            var Q66;
            {var subQ0=sQuery(id+"F0.wireOp",EDGE,"E251");Q66=makeQuery(id+"F0.imprint","IMPRINT",FACE,{"disambiguationData":[TD([[makeQuery(id+"F0.imprint","IMPRINT",EDGE,{"derivedFrom":subQ0}),-1.0]])]});}
            var Q67;
            Q67=makeQuery(id+"F0.imprint","IMPRINT",FACE,{"disambiguationData":[TD([[makeQuery(id+"F0.imprint","IMPRINT",EDGE,{"derivedFrom":sQuery(id+"F0.wireOp",EDGE,"E252")}),-1.0]])]});
            var Q68;
            {var subQ0=sQuery(id+"F0.wireOp",EDGE,"E273");Q68=makeQuery(id+"F0.imprint","IMPRINT",FACE,{"disambiguationData":[TD([[makeQuery(id+"F0.imprint","IMPRINT",EDGE,{"derivedFrom":subQ0}),-1.0]])]});}
            var Q69;
            Q69=makeQuery(id+"F0.imprint","IMPRINT",FACE,{"disambiguationData":[TD([[makeQuery(id+"F0.imprint","IMPRINT",EDGE,{"derivedFrom":sQuery(id+"F0.wireOp",EDGE,"E274")}),-1.0]])]});
            var Q70;
            Q70=makeQuery(id+"F0.imprint","IMPRINT",FACE,{"disambiguationData":[TD([[makeQuery(id+"F0.imprint","IMPRINT",EDGE,{"derivedFrom":sQuery(id+"F0.wireOp",EDGE,"E276")}),-1.0]])]});
            var Q71;
            {var subQ0=sQuery(id+"F0.wireOp",EDGE,"E267");Q71=makeQuery(id+"F0.imprint","IMPRINT",FACE,{"disambiguationData":[TD([[makeQuery(id+"F0.imprint","IMPRINT",EDGE,{"derivedFrom":subQ0}),-1.0]])]});}
            var Q72;
            {var subQ0=sQuery(id+"F0.wireOp",EDGE,"E268");Q72=makeQuery(id+"F0.imprint","IMPRINT",FACE,{"disambiguationData":[TD([[makeQuery(id+"F0.imprint","IMPRINT",EDGE,{"derivedFrom":subQ0}),-1.0]])]});}
            var Q73;
            {var subQ0=sQuery(id+"F0.wireOp",EDGE,"E323");Q73=makeQuery(id+"F0.imprint","IMPRINT",FACE,{"disambiguationData":[TD([[makeQuery(id+"F0.imprint","IMPRINT",EDGE,{"derivedFrom":subQ0}),-1.0]])]});}
            var Q74;
            Q74=makeQuery(id+"F0.imprint","IMPRINT",FACE,{"disambiguationData":[TD([[makeQuery(id+"F0.imprint","IMPRINT",EDGE,{"derivedFrom":sQuery(id+"F0.wireOp",EDGE,"E324")}),-1.0]])]});
            var Q75;
            Q75=makeQuery(id+"F0.imprint","IMPRINT",FACE,{"disambiguationData":[TD([[makeQuery(id+"F0.imprint","IMPRINT",EDGE,{"derivedFrom":sQuery(id+"F0.wireOp",EDGE,"E330")}),-1.0]])]});
            var Q76;
            {var subQ0=sQuery(id+"F0.wireOp",EDGE,"E316");Q76=makeQuery(id+"F0.imprint","IMPRINT",FACE,{"disambiguationData":[TD([[makeQuery(id+"F0.imprint","IMPRINT",EDGE,{"derivedFrom":subQ0}),-1.0]])]});}
            var Q77;
            {var subQ0=sQuery(id+"F0.wireOp",EDGE,"E317");Q77=makeQuery(id+"F0.imprint","IMPRINT",FACE,{"disambiguationData":[TD([[makeQuery(id+"F0.imprint","IMPRINT",EDGE,{"derivedFrom":subQ0}),-1.0]])]});}
            var Q78;
            {var subQ0=sQuery(id+"F0.wireOp",EDGE,"E338");Q78=makeQuery(id+"F0.imprint","IMPRINT",FACE,{"disambiguationData":[TD([[makeQuery(id+"F0.imprint","IMPRINT",EDGE,{"derivedFrom":subQ0}),-1.0]])]});}
            var Q79;
            Q79=makeQuery(id+"F0.imprint","IMPRINT",FACE,{"disambiguationData":[TD([[makeQuery(id+"F0.imprint","IMPRINT",EDGE,{"derivedFrom":sQuery(id+"F0.wireOp",EDGE,"E339")}),-1.0]])]});
            var Q80;
            Q80=makeQuery(id+"F0.imprint","IMPRINT",FACE,{"disambiguationData":[TD([[makeQuery(id+"F0.imprint","IMPRINT",EDGE,{"derivedFrom":sQuery(id+"F0.wireOp",EDGE,"E344")}),-1.0]])]});
            var Q81;
            {var subQ0=sQuery(id+"F0.wireOp",EDGE,"E331");Q81=makeQuery(id+"F0.imprint","IMPRINT",FACE,{"disambiguationData":[TD([[makeQuery(id+"F0.imprint","IMPRINT",EDGE,{"derivedFrom":subQ0}),-1.0]])]});}
            var Q82;
            {var subQ0=sQuery(id+"F0.wireOp",EDGE,"E332");Q82=makeQuery(id+"F0.imprint","IMPRINT",FACE,{"disambiguationData":[TD([[makeQuery(id+"F0.imprint","IMPRINT",EDGE,{"derivedFrom":subQ0}),-1.0]])]});}
            var Q83;
            {var subQ0=sQuery(id+"F0.wireOp",EDGE,"E363");Q83=makeQuery(id+"F0.imprint","IMPRINT",FACE,{"disambiguationData":[TD([[makeQuery(id+"F0.imprint","IMPRINT",EDGE,{"derivedFrom":subQ0}),-1.0]])]});}
            var Q84;
            Q84=makeQuery(id+"F0.imprint","IMPRINT",FACE,{"disambiguationData":[TD([[makeQuery(id+"F0.imprint","IMPRINT",EDGE,{"derivedFrom":sQuery(id+"F0.wireOp",EDGE,"E364")}),-1.0]])]});
            var Q85;
            Q85=makeQuery(id+"F0.imprint","IMPRINT",FACE,{"disambiguationData":[TD([[makeQuery(id+"F0.imprint","IMPRINT",EDGE,{"derivedFrom":sQuery(id+"F0.wireOp",EDGE,"E370")}),-1.0]])]});
            var Q86;
            {var subQ0=sQuery(id+"F0.wireOp",EDGE,"E356");Q86=makeQuery(id+"F0.imprint","IMPRINT",FACE,{"disambiguationData":[TD([[makeQuery(id+"F0.imprint","IMPRINT",EDGE,{"derivedFrom":subQ0}),-1.0]])]});}
            var Q87;
            {var subQ0=sQuery(id+"F0.wireOp",EDGE,"E357");Q87=makeQuery(id+"F0.imprint","IMPRINT",FACE,{"disambiguationData":[TD([[makeQuery(id+"F0.imprint","IMPRINT",EDGE,{"derivedFrom":subQ0}),-1.0]])]});}
            var Q88;
            {var subQ0=sQuery(id+"F0.wireOp",EDGE,"E378");Q88=makeQuery(id+"F0.imprint","IMPRINT",FACE,{"disambiguationData":[TD([[makeQuery(id+"F0.imprint","IMPRINT",EDGE,{"derivedFrom":subQ0}),-1.0]])]});}
            var Q89;
            Q89=makeQuery(id+"F0.imprint","IMPRINT",FACE,{"disambiguationData":[TD([[makeQuery(id+"F0.imprint","IMPRINT",EDGE,{"derivedFrom":sQuery(id+"F0.wireOp",EDGE,"E379")}),-1.0]])]});
            var Q90;
            Q90=makeQuery(id+"F0.imprint","IMPRINT",FACE,{"disambiguationData":[TD([[makeQuery(id+"F0.imprint","IMPRINT",EDGE,{"derivedFrom":sQuery(id+"F0.wireOp",EDGE,"E384")}),-1.0]])]});
            var Q91;
            {var subQ0=sQuery(id+"F0.wireOp",EDGE,"E371");Q91=makeQuery(id+"F0.imprint","IMPRINT",FACE,{"disambiguationData":[TD([[makeQuery(id+"F0.imprint","IMPRINT",EDGE,{"derivedFrom":subQ0}),-1.0]])]});}
            var Q92;
            {var subQ0=sQuery(id+"F0.wireOp",EDGE,"E372");Q92=makeQuery(id+"F0.imprint","IMPRINT",FACE,{"disambiguationData":[TD([[makeQuery(id+"F0.imprint","IMPRINT",EDGE,{"derivedFrom":subQ0}),-1.0]])]});}
            var Q93;
            {var subQ0=sQuery(id+"F0.wireOp",EDGE,"E393");Q93=makeQuery(id+"F0.imprint","IMPRINT",FACE,{"disambiguationData":[TD([[makeQuery(id+"F0.imprint","IMPRINT",EDGE,{"derivedFrom":subQ0}),-1.0]])]});}
            var Q94;
            Q94=makeQuery(id+"F0.imprint","IMPRINT",FACE,{"disambiguationData":[TD([[makeQuery(id+"F0.imprint","IMPRINT",EDGE,{"derivedFrom":sQuery(id+"F0.wireOp",EDGE,"E394")}),-1.0]])]});
            var Q95;
            Q95=makeQuery(id+"F0.imprint","IMPRINT",FACE,{"disambiguationData":[TD([[makeQuery(id+"F0.imprint","IMPRINT",EDGE,{"derivedFrom":sQuery(id+"F0.wireOp",EDGE,"E400")}),-1.0]])]});
            var Q96;
            {var subQ0=sQuery(id+"F0.wireOp",EDGE,"E386");Q96=makeQuery(id+"F0.imprint","IMPRINT",FACE,{"disambiguationData":[TD([[makeQuery(id+"F0.imprint","IMPRINT",EDGE,{"derivedFrom":subQ0}),-1.0]])]});}
            var Q97;
            Q97=makeQuery(id+"F0.imprint","IMPRINT",FACE,{"disambiguationData":[TD([[makeQuery(id+"F0.imprint","IMPRINT",EDGE,{"derivedFrom":sQuery(id+"F0.wireOp",EDGE,"E387")}),-1.0]])]});
            var Q98;
            {var subQ0=sQuery(id+"F0.wireOp",EDGE,"E405");Q98=makeQuery(id+"F0.imprint","IMPRINT",FACE,{"disambiguationData":[TD([[makeQuery(id+"F0.imprint","IMPRINT",EDGE,{"derivedFrom":subQ0}),-1.0]])]});}
            var Q99;
            Q99=makeQuery(id+"F0.imprint","IMPRINT",FACE,{"disambiguationData":[TD([[makeQuery(id+"F0.imprint","IMPRINT",EDGE,{"derivedFrom":sQuery(id+"F0.wireOp",EDGE,"E406")}),-1.0]])]});
            var Q100;
            Q100=makeQuery(id+"F0.imprint","IMPRINT",FACE,{"disambiguationData":[TD([[makeQuery(id+"F0.imprint","IMPRINT",EDGE,{"derivedFrom":sQuery(id+"F0.wireOp",EDGE,"E413")}),-1.0]])]});
            var Q101;
            {var subQ4=sQuery(id+"F0.wireOp",EDGE,"E401");Q101=makeQuery(id+"F0.imprint","IMPRINT",FACE,{"disambiguationData":[TD([[makeQuery(id+"F0.imprint","IMPRINT",EDGE,{"derivedFrom":subQ4}),1.0]])]});}
            var Q102;
            Q102=makeQuery(id+"F0.imprint","IMPRINT",FACE,{"disambiguationData":[TD([[makeQuery(id+"F0.imprint","IMPRINT",EDGE,{"derivedFrom":sQuery(id+"F0.wireOp",EDGE,"E402")}),1.0]])]});
            var Q103;
            {var subQ2=sQuery(id+"F0.wireOp",EDGE,"E454");Q103=makeQuery(id+"F0.imprint","IMPRINT",FACE,{"disambiguationData":[TD([[makeQuery(id+"F0.imprint","IMPRINT",EDGE,{"derivedFrom":subQ2}),-1.0]])]});}
            var Q104;
            {var subQ3=sQuery(id+"F0.wireOp",EDGE,"E432");Q104=makeQuery(id+"F0.imprint","IMPRINT",FACE,{"disambiguationData":[TD([[makeQuery(id+"F0.imprint","IMPRINT",EDGE,{"derivedFrom":subQ3}),1.0]])]});}
            var Q105;
            Q105=makeQuery(id+"F0.imprint","IMPRINT",FACE,{"disambiguationData":[TD([[makeQuery(id+"F0.imprint","IMPRINT",EDGE,{"derivedFrom":sQuery(id+"F0.wireOp",EDGE,"E433")}),1.0]])]});
            var Q106;
            {var subQ0=sQuery(id+"F0.wireOp",EDGE,"E456");Q106=makeQuery(id+"F0.imprint","IMPRINT",FACE,{"disambiguationData":[TD([[makeQuery(id+"F0.imprint","IMPRINT",EDGE,{"derivedFrom":subQ0}),1.0]])]});}
            var Q107;
            Q107=makeQuery(id+"F0.imprint","IMPRINT",FACE,{"disambiguationData":[TD([[makeQuery(id+"F0.imprint","IMPRINT",EDGE,{"derivedFrom":sQuery(id+"F0.wireOp",EDGE,"E0")}),-1.0]])]});
            var Q108;
            {var subQ0=sQuery(id+"F0.wireOp",EDGE,"E461");Q108=makeQuery(id+"F0.imprint","IMPRINT",FACE,{"disambiguationData":[TD([[makeQuery(id+"F0.imprint","IMPRINT",EDGE,{"derivedFrom":subQ0}),1.0]])]});}
            var Q109;
            Q109=makeQuery(id+"F0.imprint","IMPRINT",FACE,{"disambiguationData":[TD([[makeQuery(id+"F0.imprint","IMPRINT",EDGE,{"derivedFrom":sQuery(id+"F0.wireOp",EDGE,"E437")}),1.0]])]});
            var Q110;
            {var subQ0=sQuery(id+"F0.wireOp",EDGE,"E464");Q110=makeQuery(id+"F0.imprint","IMPRINT",FACE,{"disambiguationData":[TD([[makeQuery(id+"F0.imprint","IMPRINT",EDGE,{"derivedFrom":subQ0}),1.0]])]});}
            var Q111;
            Q111=makeQuery(id+"F0.imprint","IMPRINT",FACE,{"disambiguationData":[TD([[makeQuery(id+"F0.imprint","IMPRINT",EDGE,{"derivedFrom":sQuery(id+"F0.wireOp",EDGE,"E438")}),1.0]])]});
            var Q112;
            {var subQ0=sQuery(id+"F0.wireOp",EDGE,"E466");Q112=makeQuery(id+"F0.imprint","IMPRINT",FACE,{"disambiguationData":[TD([[makeQuery(id+"F0.imprint","IMPRINT",EDGE,{"derivedFrom":subQ0}),1.0]])]});}
            var Q113;
            Q113=makeQuery(id+"F0.imprint","IMPRINT",FACE,{"disambiguationData":[TD([[makeQuery(id+"F0.imprint","IMPRINT",EDGE,{"derivedFrom":sQuery(id+"F0.wireOp",EDGE,"E439")}),1.0]])]});
            var Q114;
            {var subQ3=sQuery(id+"F0.wireOp",EDGE,"E470");Q114=makeQuery(id+"F0.imprint","IMPRINT",FACE,{"disambiguationData":[TD([[makeQuery(id+"F0.imprint","IMPRINT",EDGE,{"derivedFrom":subQ3}),1.0]])]});}
            var Q115;
            Q115=makeQuery(id+"F0.imprint","IMPRINT",FACE,{"disambiguationData":[TD([[makeQuery(id+"F0.imprint","IMPRINT",EDGE,{"derivedFrom":sQuery(id+"F0.wireOp",EDGE,"E440")}),1.0]])]});
            var Q116;
            {var subQ0=sQuery(id+"F0.wireOp",EDGE,"E474");Q116=makeQuery(id+"F0.imprint","IMPRINT",FACE,{"disambiguationData":[TD([[makeQuery(id+"F0.imprint","IMPRINT",EDGE,{"derivedFrom":subQ0}),1.0]])]});}
            var Q117;
            Q117=makeQuery(id+"F0.imprint","IMPRINT",FACE,{"disambiguationData":[TD([[makeQuery(id+"F0.imprint","IMPRINT",EDGE,{"derivedFrom":sQuery(id+"F0.wireOp",EDGE,"E441")}),1.0]])]});
            var Q118;
            {var subQ0=sQuery(id+"F0.wireOp",EDGE,"E482");Q118=makeQuery(id+"F0.imprint","IMPRINT",FACE,{"disambiguationData":[TD([[makeQuery(id+"F0.imprint","IMPRINT",EDGE,{"derivedFrom":subQ0}),-1.0]])]});}
            var Q119;
            Q119=makeQuery(id+"F0.imprint","IMPRINT",FACE,{"disambiguationData":[TD([[makeQuery(id+"F0.imprint","IMPRINT",EDGE,{"derivedFrom":sQuery(id+"F0.wireOp",EDGE,"E442")}),1.0]])]});
            var Q120;
            {var subQ0=sQuery(id+"F0.wireOp",EDGE,"E481");Q120=makeQuery(id+"F0.imprint","IMPRINT",FACE,{"disambiguationData":[TD([[makeQuery(id+"F0.imprint","IMPRINT",EDGE,{"derivedFrom":subQ0}),1.0]])]});}
            var Q121;
            Q121=makeQuery(id+"F0.imprint","IMPRINT",FACE,{"disambiguationData":[TD([[makeQuery(id+"F0.imprint","IMPRINT",EDGE,{"derivedFrom":sQuery(id+"F0.wireOp",EDGE,"E443")}),1.0]])]});
            var Q122;
            {var subQ0=sQuery(id+"F0.wireOp",EDGE,"E487");Q122=makeQuery(id+"F0.imprint","IMPRINT",FACE,{"disambiguationData":[TD([[makeQuery(id+"F0.imprint","IMPRINT",EDGE,{"derivedFrom":subQ0}),1.0]])]});}
            var Q123;
            Q123=makeQuery(id+"F0.imprint","IMPRINT",FACE,{"disambiguationData":[TD([[makeQuery(id+"F0.imprint","IMPRINT",EDGE,{"derivedFrom":sQuery(id+"F0.wireOp",EDGE,"E451")}),1.0]])]});
            var Q124;
            Q124=makeQuery(id+"F0.imprint","IMPRINT",FACE,{"disambiguationData":[TD([[makeQuery(id+"F0.imprint","IMPRINT",EDGE,{"derivedFrom":sQuery(id+"F0.wireOp",EDGE,"E1")}),1.0]])]});
            var Q125;
            Q125=makeQuery(id+"F0.imprint","IMPRINT",FACE,{"disambiguationData":[TD([[makeQuery(id+"F0.imprint","IMPRINT",EDGE,{"derivedFrom":sQuery(id+"F0.wireOp",EDGE,"E452")}),1.0]])]});
            var Q126;
            {var subQ0=sQuery(id+"F0.wireOp",EDGE,"E493");Q126=makeQuery(id+"F0.imprint","IMPRINT",FACE,{"disambiguationData":[TD([[makeQuery(id+"F0.imprint","IMPRINT",EDGE,{"derivedFrom":subQ0}),1.0]])]});}
            var Q127;
            {var subQ0=sQuery(id+"F0.wireOp",EDGE,"E3");Q127=makeQuery(id+"F0.imprint","IMPRINT",FACE,{"disambiguationData":[TD([[makeQuery(id+"F0.imprint","IMPRINT",EDGE,{"derivedFrom":subQ0}),-1.0]])]});}
            var Q128;
            {var subQ0=sQuery(id+"F0.wireOp",EDGE,"E2");Q128=makeQuery(id+"F0.imprint","IMPRINT",FACE,{"disambiguationData":[TD([[makeQuery(id+"F0.imprint","IMPRINT",EDGE,{"derivedFrom":subQ0}),1.0]])]});}
            var Q129;
            Q129=makeQuery(id+"F0.imprint","IMPRINT",FACE,{"disambiguationData":[TD([[makeQuery(id+"F0.imprint","IMPRINT",EDGE,{"derivedFrom":sQuery(id+"F0.wireOp",EDGE,"E5")}),-1.0]])]});
            var Q130;
            Q130=makeQuery(id+"F0.imprint","IMPRINT",FACE,{"disambiguationData":[TD([[makeQuery(id+"F0.imprint","IMPRINT",EDGE,{"derivedFrom":sQuery(id+"F0.wireOp",EDGE,"E289")}),-1.0]])]});
            var Q131;
            Q131=makeQuery(id+"F0.imprint","IMPRINT",FACE,{"disambiguationData":[TD([[makeQuery(id+"F0.imprint","IMPRINT",EDGE,{"derivedFrom":sQuery(id+"F0.wireOp",EDGE,"E295")}),-1.0]])]});
            var Q132;
            Q132=makeQuery(id+"F0.imprint","IMPRINT",FACE,{"disambiguationData":[TD([[makeQuery(id+"F0.imprint","IMPRINT",EDGE,{"derivedFrom":sQuery(id+"F0.wireOp",EDGE,"E282")}),-1.0]])]});
            var Q133;
            {var subQ0=sQuery(id+"F0.wireOp",EDGE,"E283");Q133=makeQuery(id+"F0.imprint","IMPRINT",FACE,{"disambiguationData":[TD([[makeQuery(id+"F0.imprint","IMPRINT",EDGE,{"derivedFrom":subQ0}),-1.0]])]});}
            var Q134;
            Q134=makeQuery(id+"F0.imprint","IMPRINT",FACE,{"disambiguationData":[TD([[makeQuery(id+"F0.imprint","IMPRINT",EDGE,{"derivedFrom":sQuery(id+"F0.wireOp",EDGE,"E4")}),-1.0]])]});
            var Q135;
            Q135=makeQuery(id+"F0.imprint","IMPRINT",FACE,{"disambiguationData":[TD([[makeQuery(id+"F0.imprint","IMPRINT",EDGE,{"derivedFrom":sQuery(id+"F0.wireOp",EDGE,"E304")}),-1.0]])]});
            var Q136;
            {var subQ0=sQuery(id+"F0.wireOp",EDGE,"E310");Q136=makeQuery(id+"F0.imprint","IMPRINT",FACE,{"disambiguationData":[TD([[makeQuery(id+"F0.imprint","IMPRINT",EDGE,{"derivedFrom":subQ0}),-1.0]])]});}
            var Q137;
            {var subQ0=sQuery(id+"F0.wireOp",EDGE,"E296");Q137=makeQuery(id+"F0.imprint","IMPRINT",FACE,{"disambiguationData":[TD([[makeQuery(id+"F0.imprint","IMPRINT",EDGE,{"derivedFrom":subQ0}),-1.0]])]});}
            var Q138;
            {var subQ0=sQuery(id+"F0.wireOp",EDGE,"E297");Q138=makeQuery(id+"F0.imprint","IMPRINT",FACE,{"disambiguationData":[TD([[makeQuery(id+"F0.imprint","IMPRINT",EDGE,{"derivedFrom":subQ0}),-1.0]])]});}
            var Q139;
            {var subQ0=sQuery(id+"F0.wireOp",EDGE,"E349");Q139=makeQuery(id+"F0.imprint","IMPRINT",FACE,{"disambiguationData":[TD([[makeQuery(id+"F0.imprint","IMPRINT",EDGE,{"derivedFrom":subQ0}),1.0]])]});}
            var Q140;
            Q140=makeQuery(id+"F0.imprint","IMPRINT",FACE,{"disambiguationData":[TD([[makeQuery(id+"F0.imprint","IMPRINT",EDGE,{"derivedFrom":sQuery(id+"F0.wireOp",EDGE,"E347")}),-1.0]])]});
            var Q141;
            Q141=makeQuery(id+"F0.imprint","IMPRINT",FACE,{"disambiguationData":[TD([[makeQuery(id+"F0.imprint","IMPRINT",EDGE,{"derivedFrom":sQuery(id+"F0.wireOp",EDGE,"E352")}),-1.0]])]});
            var Q142;
            {var subQ0=sQuery(id+"F0.wireOp",EDGE,"E513");Q142=makeQuery(id+"F0.imprint","IMPRINT",FACE,{"disambiguationData":[TD([[makeQuery(id+"F0.imprint","IMPRINT",EDGE,{"derivedFrom":subQ0}),-1.0]])]});}
            var Q143;
            Q143=makeQuery(id+"F0.imprint","IMPRINT",FACE,{"disambiguationData":[TD([[makeQuery(id+"F0.imprint","IMPRINT",EDGE,{"derivedFrom":sQuery(id+"F0.wireOp",EDGE,"E514")}),-1.0]])]});
            var Q144;
            {var subQ5=sQuery(id+"F0.wireOp",EDGE,"E524");Q144=makeQuery(id+"F0.imprint","IMPRINT",FACE,{"disambiguationData":[TD([[makeQuery(id+"F0.imprint","IMPRINT",EDGE,{"derivedFrom":subQ5}),1.0]])]});}
            var Q145;
            Q145=makeQuery(id+"F0.imprint","IMPRINT",FACE,{"disambiguationData":[TD([[makeQuery(id+"F0.imprint","IMPRINT",EDGE,{"derivedFrom":sQuery(id+"F0.wireOp",EDGE,"E522")}),-1.0]])]});
            var Q146;
            Q146=makeQuery(id+"F0.imprint","IMPRINT",FACE,{"disambiguationData":[TD([[makeQuery(id+"F0.imprint","IMPRINT",EDGE,{"derivedFrom":sQuery(id+"F0.wireOp",EDGE,"E527")}),-1.0]])]});
            var Q147;
            {var subQ0=sQuery(id+"F0.wireOp",EDGE,"E532");Q147=makeQuery(id+"F0.imprint","IMPRINT",FACE,{"disambiguationData":[TD([[makeQuery(id+"F0.imprint","IMPRINT",EDGE,{"derivedFrom":subQ0}),-1.0]])]});}
            var Q148;
            Q148=makeQuery(id+"F0.imprint","IMPRINT",FACE,{"disambiguationData":[TD([[makeQuery(id+"F0.imprint","IMPRINT",EDGE,{"derivedFrom":sQuery(id+"F0.wireOp",EDGE,"E533")}),-1.0]])]});
            var Q149;
            {var subQ5=sQuery(id+"F0.wireOp",EDGE,"E543");Q149=makeQuery(id+"F0.imprint","IMPRINT",FACE,{"disambiguationData":[TD([[makeQuery(id+"F0.imprint","IMPRINT",EDGE,{"derivedFrom":subQ5}),1.0]])]});}
            var Q150;
            Q150=makeQuery(id+"F0.imprint","IMPRINT",FACE,{"disambiguationData":[TD([[makeQuery(id+"F0.imprint","IMPRINT",EDGE,{"derivedFrom":sQuery(id+"F0.wireOp",EDGE,"E541")}),-1.0]])]});
            var Q151;
            Q151=makeQuery(id+"F0.imprint","IMPRINT",FACE,{"disambiguationData":[TD([[makeQuery(id+"F0.imprint","IMPRINT",EDGE,{"derivedFrom":sQuery(id+"F0.wireOp",EDGE,"E540")}),1.0]])]});
            var Q152;
            {var subQ0=sQuery(id+"F0.wireOp",EDGE,"E551");Q152=makeQuery(id+"F0.imprint","IMPRINT",FACE,{"disambiguationData":[TD([[makeQuery(id+"F0.imprint","IMPRINT",EDGE,{"derivedFrom":subQ0}),-1.0]])]});}
            var Q153;
            Q153=makeQuery(id+"F0.imprint","IMPRINT",FACE,{"disambiguationData":[TD([[makeQuery(id+"F0.imprint","IMPRINT",EDGE,{"derivedFrom":sQuery(id+"F0.wireOp",EDGE,"E552")}),-1.0]])]});
            var Q154;
            {var subQ5=sQuery(id+"F0.wireOp",EDGE,"E562");Q154=makeQuery(id+"F0.imprint","IMPRINT",FACE,{"disambiguationData":[TD([[makeQuery(id+"F0.imprint","IMPRINT",EDGE,{"derivedFrom":subQ5}),1.0]])]});}
            var Q155;
            Q155=makeQuery(id+"F0.imprint","IMPRINT",FACE,{"disambiguationData":[TD([[makeQuery(id+"F0.imprint","IMPRINT",EDGE,{"derivedFrom":sQuery(id+"F0.wireOp",EDGE,"E560")}),-1.0]])]});
            var Q156;
            Q156=makeQuery(id+"F0.imprint","IMPRINT",FACE,{"disambiguationData":[TD([[makeQuery(id+"F0.imprint","IMPRINT",EDGE,{"derivedFrom":sQuery(id+"F0.wireOp",EDGE,"E559")}),1.0]])]});
            var Q157;
            {var subQ0=sQuery(id+"F0.wireOp",EDGE,"E570");Q157=makeQuery(id+"F0.imprint","IMPRINT",FACE,{"disambiguationData":[TD([[makeQuery(id+"F0.imprint","IMPRINT",EDGE,{"derivedFrom":subQ0}),-1.0]])]});}
            var Q158;
            Q158=makeQuery(id+"F0.imprint","IMPRINT",FACE,{"disambiguationData":[TD([[makeQuery(id+"F0.imprint","IMPRINT",EDGE,{"derivedFrom":sQuery(id+"F0.wireOp",EDGE,"E571")}),-1.0]])]});
            var Q159;
            Q159=makeQuery(id+"F0.imprint","IMPRINT",FACE,{"disambiguationData":[TD([[makeQuery(id+"F0.imprint","IMPRINT",EDGE,{"derivedFrom":sQuery(id+"F0.wireOp",EDGE,"E581")}),1.0]])]});
            var Q160;
            Q160=makeQuery(id+"F0.imprint","IMPRINT",FACE,{"disambiguationData":[TD([[makeQuery(id+"F0.imprint","IMPRINT",EDGE,{"derivedFrom":sQuery(id+"F0.wireOp",EDGE,"E579")}),-1.0]])]});
            var Q161;
            Q161=makeQuery(id+"F0.imprint","IMPRINT",FACE,{"disambiguationData":[TD([[makeQuery(id+"F0.imprint","IMPRINT",EDGE,{"derivedFrom":sQuery(id+"F0.wireOp",EDGE,"E578")}),1.0]])]});
            var Q162;
            {var subQ0=sQuery(id+"F0.wireOp",EDGE,"E589");Q162=makeQuery(id+"F0.imprint","IMPRINT",FACE,{"disambiguationData":[TD([[makeQuery(id+"F0.imprint","IMPRINT",EDGE,{"derivedFrom":subQ0}),-1.0]])]});}
            var Q163;
            Q163=makeQuery(id+"F0.imprint","IMPRINT",FACE,{"disambiguationData":[TD([[makeQuery(id+"F0.imprint","IMPRINT",EDGE,{"derivedFrom":sQuery(id+"F0.wireOp",EDGE,"E590")}),-1.0]])]});
            var Q164;
            {var subQ0=sQuery(id+"F0.wireOp",EDGE,"E600");Q164=makeQuery(id+"F0.imprint","IMPRINT",FACE,{"disambiguationData":[TD([[makeQuery(id+"F0.imprint","IMPRINT",EDGE,{"derivedFrom":subQ0}),1.0]])]});}
            var Q165;
            Q165=makeQuery(id+"F0.imprint","IMPRINT",FACE,{"disambiguationData":[TD([[makeQuery(id+"F0.imprint","IMPRINT",EDGE,{"derivedFrom":sQuery(id+"F0.wireOp",EDGE,"E598")}),-1.0]])]});
            var Q166;
            Q166=makeQuery(id+"F0.imprint","IMPRINT",FACE,{"disambiguationData":[TD([[makeQuery(id+"F0.imprint","IMPRINT",EDGE,{"derivedFrom":sQuery(id+"F0.wireOp",EDGE,"E597")}),1.0]])]});
            var Q167;
            {var subQ4=sQuery(id+"F0.wireOp",EDGE,"E608");Q167=makeQuery(id+"F0.imprint","IMPRINT",FACE,{"disambiguationData":[TD([[makeQuery(id+"F0.imprint","IMPRINT",EDGE,{"derivedFrom":subQ4}),1.0]])]});}
            var Q168;
            Q168=makeQuery(id+"F0.imprint","IMPRINT",FACE,{"disambiguationData":[TD([[makeQuery(id+"F0.imprint","IMPRINT",EDGE,{"derivedFrom":sQuery(id+"F0.wireOp",EDGE,"E609")}),1.0]])]});
            var Q169;
            Q169=makeQuery(id+"F0.imprint","IMPRINT",FACE,{"disambiguationData":[TD([[makeQuery(id+"F0.imprint","IMPRINT",EDGE,{"derivedFrom":sQuery(id+"F0.wireOp",EDGE,"E620")}),-1.0]])]});
            var Q170;
            {var subQ0=sQuery(id+"F0.wireOp",EDGE,"E631");Q170=makeQuery(id+"F0.imprint","IMPRINT",FACE,{"disambiguationData":[TD([[makeQuery(id+"F0.imprint","IMPRINT",EDGE,{"derivedFrom":subQ0}),-1.0]])]});}
            var Q171;
            {var subQ0=sQuery(id+"F0.wireOp",EDGE,"E632");Q171=makeQuery(id+"F0.imprint","IMPRINT",FACE,{"disambiguationData":[TD([[makeQuery(id+"F0.imprint","IMPRINT",EDGE,{"derivedFrom":subQ0}),-1.0]])]});}
            var Q172;
            Q172=makeQuery(id+"F0.imprint","IMPRINT",FACE,{"disambiguationData":[TD([[makeQuery(id+"F0.imprint","IMPRINT",EDGE,{"derivedFrom":sQuery(id+"F0.wireOp",EDGE,"E634")}),-1.0]])]});
            extrude(context, id + "F1", {"entities" : qUnion([Q0, Q1, Q2, Q3, Q4, Q5, Q6, Q7, Q8, Q9, Q10, Q11, Q12, Q13, Q14, Q15, Q16, Q17, Q18, Q19, Q20, Q21, Q22, Q23, Q24, Q25, Q26, Q27, Q28, Q29, Q30, Q31, Q32, Q33, Q34, Q35, Q36, Q37, Q38, Q39, Q40, Q41, Q42, Q43, Q44, Q45, Q46, Q47, Q48, Q49, Q50, Q51, Q52, Q53, Q54, Q55, Q56, Q57, Q58, Q59, Q60, Q61, Q62, Q63, Q64, Q65, Q66, Q67, Q68, Q69, Q70, Q71, Q72, Q73, Q74, Q75, Q76, Q77, Q78, Q79, Q80, Q81, Q82, Q83, Q84, Q85, Q86, Q87, Q88, Q89, Q90, Q91, Q92, Q93, Q94, Q95, Q96, Q97, Q98, Q99, Q100, Q101, Q102, Q103, Q104, Q105, Q106, Q107, Q108, Q109, Q110, Q111, Q112, Q113, Q114, Q115, Q116, Q117, Q118, Q119, Q120, Q121, Q122, Q123, Q124, Q125, Q126, Q127, Q128, Q129, Q130, Q131, Q132, Q133, Q134, Q135, Q136, Q137, Q138, Q139, Q140, Q141, Q142, Q143, Q144, Q145, Q146, Q147, Q148, Q149, Q150, Q151, Q152, Q153, Q154, Q155, Q156, Q157, Q158, Q159, Q160, Q161, Q162, Q163, Q164, Q165, Q166, Q167, Q168, Q169, Q170, Q171, Q172]), "depth" : 10 * mm, "hasSecondDirection" : true, "secondDirectionOppositeDirection" : true, "secondDirectionDepth" : 800 * mm});
        }
        {
            var Q0;
            {var subQ7=sQuery(id+"F0.wireOp",EDGE,"E638");Q0=makeQuery(id+"F0.imprint","IMPRINT",FACE,{"disambiguationData":[TD([[makeQuery(id+"F0.imprint","IMPRINT",EDGE,{"derivedFrom":subQ7}),-1.0]])]});}
            extrude(context, id + "F2", {"entities" : qUnion([Q0]), "depth" : 25 * mm, "hasSecondDirection" : true, "secondDirectionOppositeDirection" : true, "secondDirectionDepth" : 600 * mm});
        }
        {
            var Q0;
            {var subQ11=sQuery(id+"F0.wireOp",EDGE,"E615");var subQ21=makeQuery(id+"F0.imprint","INTERSECT",VERTEX,{"derivedFrom":[sQuery(id+"F0.wireOp",EDGE,"E155"),subQ11]});Q0=makeQuery(id+"F0.imprint","IMPRINT",FACE,{"disambiguationData":[TD([[makeQuery(id+"F0.imprint","IMPRINT",EDGE,{"disambiguationData":[TD([[subQ21,-1.0]])],"derivedFrom":subQ11}),-1.0]])]});}
            extrude(context, id + "F3", {"entities" : qUnion([Q0]), "depth" : 100 * mm});
        }
        {
            var Q0;
            {var subQ8=sQuery(id+"F0.wireOp",EDGE,"E8");Q0=makeQuery(id+"F0.imprint","IMPRINT",FACE,{"disambiguationData":[TD([[makeQuery(id+"F0.imprint","IMPRINT",EDGE,{"derivedFrom":subQ8}),1.0]])]});}
            extrude(context, id + "F4", {"entities" : qUnion([Q0]), "depth" : 510 * mm, "hasSecondDirection" : true, "secondDirectionOppositeDirection" : true, "secondDirectionDepth" : 800 * mm});
        }
        {
            var Q0;
            Q0=makeQuery(id+"F0.imprint","IMPRINT",FACE,{"disambiguationData":[TD([[makeQuery(id+"F0.imprint","IMPRINT",EDGE,{"derivedFrom":sQuery(id+"F0.wireOp",EDGE,"E0")}),1.0]])]});
            extrude(context, id + "F5", {"entities" : qUnion([Q0]), "depth" : 1 * mm});
        }
    });
